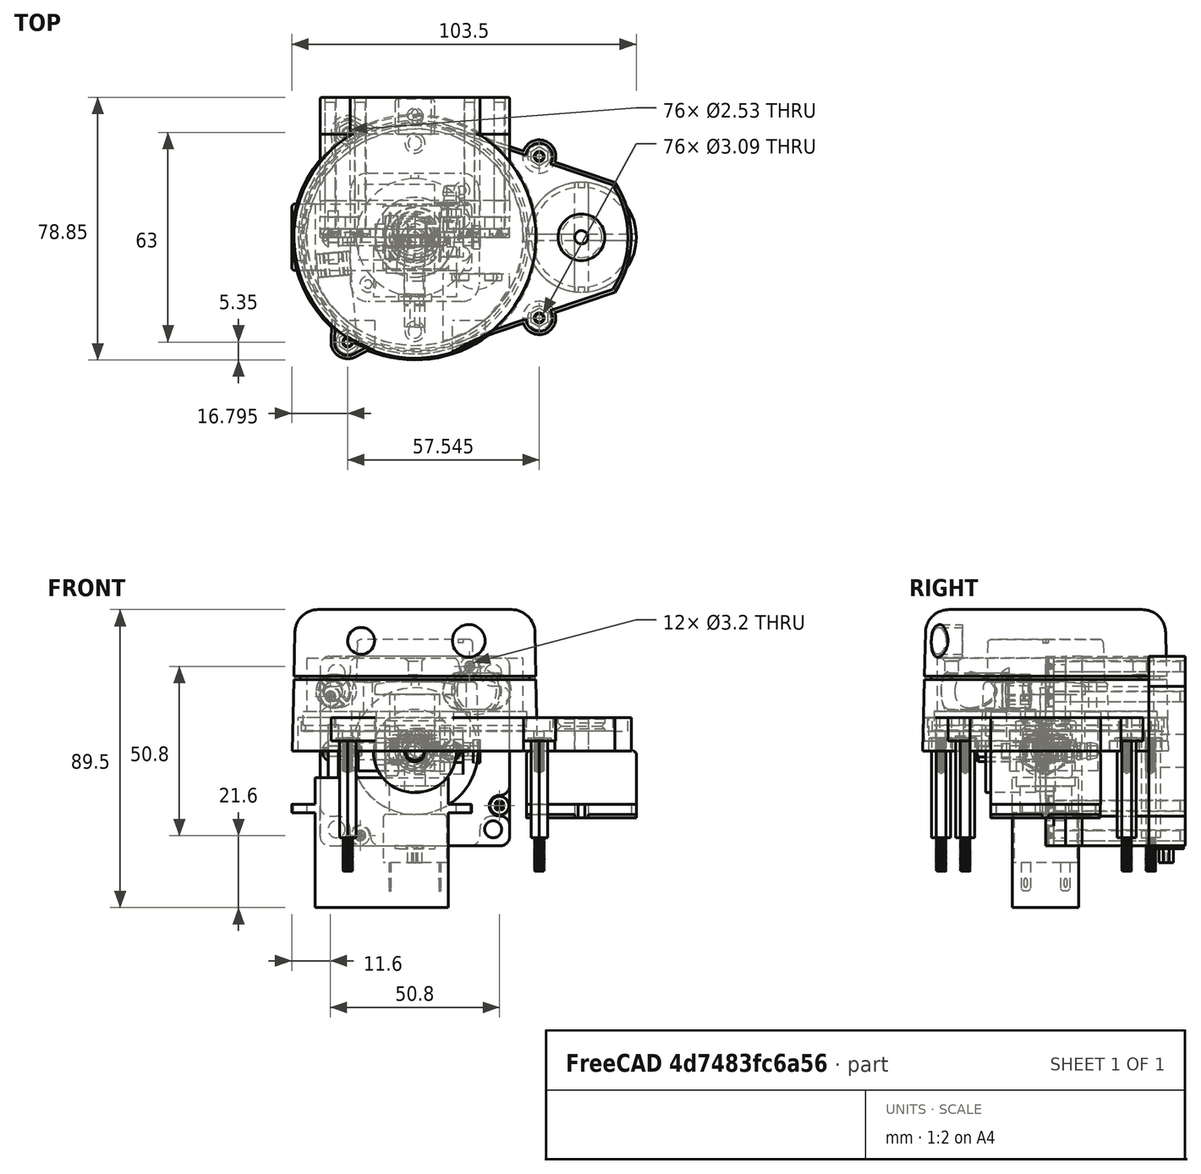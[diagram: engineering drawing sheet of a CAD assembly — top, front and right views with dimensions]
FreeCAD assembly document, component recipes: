
FREECAD ASSEMBLY — COMPONENT RECIPES ("generic-hardware")

This assembly document has 22 components, labeled P0..P21 below (a component is one placed body or linked part). 20 of them carry a construction recipe — the FreeCAD feature program that regenerates the part from scratch, quoted from this document or its linked companion documents; the rest are supplied as boundary geometry only. No exploded tour is included for this assembly.
NOTE — this tour is split across 2 documents so each fits a 32k-token context. This is document 1: the component sections continue in the remaining 1 document, each repeating the header above.
COMPONENT P0 — recipe-attached ("MKS_SERVO57B_", modeled in this document).
Construction recipe (the document's own serialized feature program — sketch geometry with constraints, then the solid features built on it; lengths are millimeters unless a unit is written):

FEATURE [Sketcher::SketchObject] Sketch
  ArcFitTolerance = 0
  AttachmentSupport = -> [XY_Plane]
  ExternalBSplineMaxDegree = 0
  ExternalBSplineTolerance = 0
  FullyConstrained = true
  InternalTolerance = 1e-06
  MakeInternals = false
  MapMode = 5
  Support = -> [XY_Plane]
  TreeRank = 0
  sketch-geometry (8):
    g0: LineSegment StartX=-28 StartY=0 StartZ=0 EndX=-28 EndY=18.5 EndZ=0
    g1: LineSegment StartX=-28 StartY=18.5 StartZ=0 EndX=-18.5 EndY=18.5 EndZ=0
    g2: LineSegment StartX=-18.5 StartY=18.5 StartZ=0 EndX=-18.5 EndY=28 EndZ=0
    g3: LineSegment StartX=-18.5 StartY=28 StartZ=0 EndX=0 EndY=28 EndZ=0
    g4: LineSegment StartX=0 StartY=28 StartZ=0 EndX=0 EndY=0 EndZ=0
    g5: LineSegment StartX=0 StartY=0 StartZ=0 EndX=-28 EndY=0 EndZ=0
    g6: Circle CenterX=-16 CenterY=25.5 CenterZ=0 NormalX=0 NormalY=0 NormalZ=1 AngleXU=0 Radius=1.55
    g7: Circle CenterX=-25.5 CenterY=16 CenterZ=0 NormalX=0 NormalY=0 NormalZ=1 AngleXU=0 Radius=1.55
  constraints (23):
    c: PointOnObject(g0,g-1)
    c: Vertical(g0)
    c: Coincident(g0,g1)
    c: Coincident(g1,g2)
    c: Vertical(g2)
    c: Coincident(g2,g3)
    c: PointOnObject(g3,g-2)
    c: Horizontal(g3)
    c: Coincident(g3,g4)
    c: Coincident(g4,g-1)
    c: Coincident(g4,g5)
    c: Coincident(g5,g0)
    c: Horizontal(g1)
    c: Equal(g2,g1)
    c: DistanceX(g5,g5) = 28
    c: Equal(g4,g5)
    c: DistanceX(g1,g1) = 9.5
    c: Equal(g7,g6)
    c: Diameter(g6) = 3.1
    c: DistanceX(g6) = -16
    c: DistanceY(g6) = 25.5
    c: DistanceX(g7) = -25.5
    c: DistanceY(g7) = 16
FEATURE [PartDesign::Pad] Pad
  AddSubType = 0
  AutoTaperInnerAngle = false
  CheckUpToFaceLimits = true
  ClaimChildren = false
  Direction = (1,1,1)
  Fit = 0
  FitJoin = 0
  InnerFit = 0
  InnerFitJoin = 0
  Length = 20
  Length2 = 100
  NewSolid = false
  Profile = -> Sketch
  Refine = true
  Suppress = false
  TaperInnerAngle = 0
  TaperInnerAngleRev = 0
  TreeRank = 0
  Type = 0
  _ProfileBasedVersion = 0
FEATURE [PartDesign::PolarPattern] PolarPattern012
  AddSubType = 0
  Angle = 360
  Axis = -> Sketch [N_Axis]
  BaseFeature = -> Pad
  CopyShape = false
  NewSolid = false
  Occurrences = 4
  OriginalSubs = -> [Pad]
  Originals = -> [Pad]
  ParallelTransform = true
  Refine = true
  SubTransform = true
  Suppress = false
  TreeRank = 0
  _Version = 0
FEATURE [PartDesign::Fillet] Fillet004
  AddSubType = 0
  Base = -> PolarPattern012 [Edge2,Edge38,Edge11,Edge33]
  BaseFeature = -> PolarPattern012
  NewSolid = false
  Radius = 4
  Refine = true
  SupportTransform = false
  Suppress = false
  TreeRank = 0
FEATURE [PartDesign::Fillet] Fillet005
  AddSubType = 0
  Base = -> Fillet004 [Edge30,Edge58,Edge60,Edge63,Edge61,Edge55,Edge53,Edge3]
  BaseFeature = -> Fillet004
  NewSolid = false
  Radius = 2.5
  Refine = true
  SupportTransform = false
  Suppress = false
  TreeRank = 0
FEATURE [Sketcher::SketchObject] Sketch019
  ArcFitTolerance = 0
  AttachmentSupport = -> [XZ_Plane]
  ExternalBSplineMaxDegree = 0
  ExternalBSplineTolerance = 0
  FullyConstrained = true
  InternalTolerance = 1e-06
  MakeInternals = false
  MapMode = 5
  Placement = pos=(0,0,0) rot=(1,0,0;1.5708rad)
  Support = -> [XZ_Plane]
  TreeRank = 0
  sketch-geometry (4):
    g0: LineSegment StartX=-7 StartY=10 StartZ=0 EndX=11 EndY=10 EndZ=0
    g1: LineSegment StartX=11 StartY=10 StartZ=0 EndX=11 EndY=3.5 EndZ=0
    g2: LineSegment StartX=11 StartY=3.5 StartZ=0 EndX=-7 EndY=3.5 EndZ=0
    g3: LineSegment StartX=-7 StartY=3.5 StartZ=0 EndX=-7 EndY=10 EndZ=0
  constraints (12):
    c: Coincident(g0,g1)
    c: Coincident(g1,g2)
    c: Coincident(g2,g3)
    c: Coincident(g3,g0)
    c: Horizontal(g0)
    c: Horizontal(g2)
    c: Vertical(g1)
    c: Vertical(g3)
    c: DistanceY(g1,g1) = 6.5
    c: DistanceX(g0,g0) = 18
    c: DistanceX(g0) = -7
    c: DistanceY(g0) = 10
FEATURE [PartDesign::Pad] Pad012
  AddSubType = 0
  AutoTaperInnerAngle = false
  BaseFeature = -> Fillet005
  CheckUpToFaceLimits = true
  ClaimChildren = false
  Direction = (1,1,1)
  Fit = 0
  FitJoin = 0
  InnerFit = 0
  InnerFitJoin = 0
  Length = 31.5
  Length2 = 100
  NewSolid = false
  Profile = -> Sketch019
  Refine = true
  Suppress = false
  TaperInnerAngle = 0
  TaperInnerAngleRev = 0
  TreeRank = 0
  Type = 0
  _ProfileBasedVersion = 0
FEATURE [PartDesign::Body] Body  label="MKS_SERVO57B_"
  AutoGroupSolids = false
  ClaimAllChildren = false
  ExportMode = 0
  Group = -> [Sketch,Pad,PolarPattern012,Fillet004,Fillet005,Sketch019,Pad012]
  Origin = -> Origin015
  SingleSolid = true
  Tip = -> Pad012
  TreeRank = 0
  _ExportChildren = -> [Pad,PolarPattern012,Fillet004,Fillet005,Pad012]
  _GroupVersion = 1
COMPONENT P1 — recipe-attached ("Corner", modeled in this document).
Construction recipe (the document's own serialized feature program — sketch geometry with constraints, then the solid features built on it; lengths are millimeters unless a unit is written):

FEATURE [Sketcher::SketchObject] Sketch001
  ArcFitTolerance = 0
  AttachmentSupport = -> [YZ_Plane001]
  ExternalBSplineMaxDegree = 0
  ExternalBSplineTolerance = 0
  FullyConstrained = true
  InternalTolerance = 1e-06
  MakeInternals = false
  MapMode = 5
  Placement = pos=(0,0,0) rot=(0.57735,0.57735,0.57735;2.0944rad)
  Support = -> [YZ_Plane001]
  TreeRank = 0
  sketch-geometry (4):
    g0: LineSegment StartX=-5 StartY=5 StartZ=0 EndX=5 EndY=5 EndZ=0
    g1: LineSegment StartX=5 StartY=5 StartZ=0 EndX=5 EndY=-5 EndZ=0
    g2: LineSegment StartX=5 StartY=-5 StartZ=0 EndX=-5 EndY=-5 EndZ=0
    g3: LineSegment StartX=-5 StartY=-5 StartZ=0 EndX=-5 EndY=5 EndZ=0
  constraints (11):
    c: Coincident(g0,g1)
    c: Coincident(g1,g2)
    c: Coincident(g2,g3)
    c: Coincident(g3,g0)
    c: Horizontal(g0)
    c: Horizontal(g2)
    c: Vertical(g1)
    c: Vertical(g3)
    c: Symmetric(g1,g0,g-1)
    c: Equal(g0,g3)
    c: DistanceX(g0,g0) = 10
FEATURE [PartDesign::Pad] Pad001
  AddSubType = 0
  AutoTaperInnerAngle = false
  CheckUpToFaceLimits = true
  ClaimChildren = false
  Direction = (1,1,1)
  Fit = 0
  FitJoin = 0
  InnerFit = 0
  InnerFitJoin = 0
  Length = 10
  Length2 = 100
  Midplane = true
  NewSolid = false
  Placement = pos=(0,0,0) rot=(0.57735,0.57735,0.57735;2.0944rad)
  Profile = -> Sketch001
  Refine = true
  Suppress = false
  TaperInnerAngle = 0
  TaperInnerAngleRev = 0
  TreeRank = 0
  Type = 0
  _ProfileBasedVersion = 0
FEATURE [Sketcher::SketchObject] Sketch002
  ArcFitTolerance = 0
  AttachmentSupport = -> [YZ_Plane001]
  ExternalBSplineMaxDegree = 0
  ExternalBSplineTolerance = 0
  FullyConstrained = true
  InternalTolerance = 1e-06
  MakeInternals = false
  MapMode = 5
  Placement = pos=(0,0,0) rot=(0.57735,0.57735,0.57735;2.0944rad)
  Support = -> [YZ_Plane001]
  TreeRank = 0
  sketch-geometry (1):
    g0: Circle CenterX=0 CenterY=0 CenterZ=0 NormalX=0 NormalY=0 NormalZ=1 AngleXU=0 Radius=1.5
  constraints (2):
    c: Coincident(g0,g-1)
    c: Diameter(g0) = 3
FEATURE [PartDesign::Pocket] Pocket
  AddSubType = 1
  AutoTaperInnerAngle = false
  BaseFeature = -> Pad001
  CheckUpToFaceLimits = true
  ClaimChildren = false
  Fit = 0
  FitJoin = 0
  InnerFit = 0
  InnerFitJoin = 0
  Length = 5
  Length2 = 100
  Midplane = true
  NewSolid = false
  Placement = pos=(0,0,0) rot=(0.57735,0.57735,0.57735;2.0944rad)
  Profile = -> Sketch002
  Refine = true
  Suppress = false
  TaperInnerAngle = 0
  TaperInnerAngleRev = 0
  TreeRank = 0
  Type = 1
  _ProfileBasedVersion = 0
  _Version = 0
FEATURE [PartDesign::PolarPattern] PolarPattern
  AddSubType = 0
  Angle = 90
  Axis = -> Z_Axis001
  CopyShape = false
  NewSolid = false
  Occurrences = 2
  ParallelTransform = true
  Placement = pos=(0,0,0) rot=(0.57735,0.57735,0.57735;2.0944rad)
  Refine = true
  SubTransform = true
  Suppress = false
  TreeRank = 0
  _Version = 0
FEATURE [PartDesign::PolarPattern] PolarPattern001
  AddSubType = 0
  Angle = 90
  Axis = -> Y_Axis001
  CopyShape = false
  NewSolid = false
  Occurrences = 2
  ParallelTransform = true
  Placement = pos=(0,0,0) rot=(0.57735,0.57735,0.57735;2.0944rad)
  Refine = true
  SubTransform = true
  Suppress = false
  TreeRank = 0
  _Version = 0
FEATURE [PartDesign::MultiTransform] MultiTransform
  AddSubType = 0
  BaseFeature = -> Pocket
  CopyShape = false
  NewSolid = false
  OriginalSubs = -> [Pocket]
  Originals = -> [Pocket]
  ParallelTransform = true
  Placement = pos=(0,0,0) rot=(0.57735,0.57735,0.57735;2.0944rad)
  Refine = true
  SubTransform = true
  Suppress = false
  Transformations = -> [PolarPattern,PolarPattern001]
  TreeRank = 0
  _Version = 0
FEATURE [PartDesign::Plane] DatumPlane
  AttachmentOffset = pos=(0,0,5) rot=(0,0,1;0rad)
  AttachmentSupport = -> [YZ_Plane001]
  Length = 10
  MapMode = 5
  MinimumLength = 10
  MinimumWidth = 10
  Placement = pos=(5,-1.1e-15,1.1e-15) rot=(0.57735,0.57735,0.57735;2.0944rad)
  ResizeMode = 0
  Support = -> [YZ_Plane001]
  TreeRank = 0
  Width = 10
FEATURE [Sketcher::SketchObject] Sketch003
  ArcFitTolerance = 0
  AttachmentSupport = -> [DatumPlane]
  ExternalBSplineMaxDegree = 0
  ExternalBSplineTolerance = 0
  FullyConstrained = true
  InternalTolerance = 1e-06
  MakeInternals = false
  MapMode = 5
  Placement = pos=(5,-1.1e-15,1.1e-15) rot=(0.57735,0.57735,0.57735;2.0944rad)
  Support = -> [DatumPlane]
  TreeRank = 0
  sketch-geometry (1):
    g0: Circle CenterX=0 CenterY=0 CenterZ=0 NormalX=0 NormalY=0 NormalZ=1 AngleXU=0 Radius=3
  constraints (2):
    c: Coincident(g0,g-1)
    c: Diameter(g0) = 6
FEATURE [PartDesign::Pocket] Pocket001
  AddSubType = 1
  AutoTaperInnerAngle = false
  BaseFeature = -> MultiTransform
  CheckUpToFaceLimits = true
  ClaimChildren = false
  Fit = 0
  FitJoin = 0
  InnerFit = 0
  InnerFitJoin = 0
  Length = 8
  Length2 = 100
  NewSolid = false
  Placement = pos=(0,0,0) rot=(0.57735,0.57735,0.57735;2.0944rad)
  Profile = -> Sketch003
  Refine = true
  Suppress = false
  TaperInnerAngle = 0
  TaperInnerAngleRev = 0
  TreeRank = 0
  Type = 0
  _ProfileBasedVersion = 0
  _Version = 0
FEATURE [PartDesign::PolarPattern] PolarPattern002
  AddSubType = 0
  Angle = 90
  Axis = -> Y_Axis001
  CopyShape = false
  NewSolid = false
  Occurrences = 2
  ParallelTransform = true
  Placement = pos=(0,0,0) rot=(0.57735,0.57735,0.57735;2.0944rad)
  Refine = true
  SubTransform = true
  Suppress = false
  TreeRank = 0
  _Version = 0
FEATURE [PartDesign::PolarPattern] PolarPattern003
  AddSubType = 0
  Angle = 90
  Axis = -> Z_Axis001
  CopyShape = false
  NewSolid = false
  Occurrences = 2
  ParallelTransform = true
  Placement = pos=(0,0,0) rot=(0.57735,0.57735,0.57735;2.0944rad)
  Refine = true
  SubTransform = true
  Suppress = false
  TreeRank = 0
  _Version = 0
FEATURE [PartDesign::MultiTransform] MultiTransform001
  AddSubType = 0
  BaseFeature = -> Pocket001
  CopyShape = false
  NewSolid = false
  OriginalSubs = -> [Pocket001]
  Originals = -> [Pocket001]
  ParallelTransform = true
  Placement = pos=(0,0,0) rot=(0.57735,0.57735,0.57735;2.0944rad)
  Refine = true
  SubTransform = true
  Suppress = false
  Transformations = -> [PolarPattern002,PolarPattern003]
  TreeRank = 0
  _Version = 0
FEATURE [PartDesign::Body] Body001  label="Corner"
  AutoGroupSolids = false
  ClaimAllChildren = false
  ExportMode = 0
  Group = -> [Sketch001,Pad001,Sketch002,Pocket,MultiTransform,PolarPattern,PolarPattern001,DatumPlane,Sketch003,Pocket001,MultiTransform001,PolarPattern002,PolarPattern003]
  Origin = -> Origin001
  SingleSolid = true
  Tip = -> MultiTransform001
  TreeRank = 0
  _ExportChildren = -> [Pad001,Pocket,MultiTransform,DatumPlane,Pocket001,MultiTransform001]
  _GroupVersion = 1
COMPONENT P2 — recipe-attached ("MB_100", modeled in this document).
Construction recipe (the document's own serialized feature program — sketch geometry with constraints, then the solid features built on it; lengths are millimeters unless a unit is written):

FEATURE [Sketcher::SketchObject] Sketch004
  ArcFitTolerance = 0
  AttachmentSupport = -> [XZ_Plane002]
  ExternalBSplineMaxDegree = 0
  ExternalBSplineTolerance = 0
  FullyConstrained = true
  InternalTolerance = 1e-06
  MakeInternals = false
  MapMode = 5
  Placement = pos=(0,0,0) rot=(1,0,0;1.5708rad)
  Support = -> [XZ_Plane002]
  TreeRank = 0
  sketch-geometry (14):
    g0: ArcOfCircle CenterX=0 CenterY=0 CenterZ=0 NormalX=0 NormalY=0 NormalZ=1 AngleXU=0 Radius=1.25 StartAngle=0 EndAngle=1.5708
    g1: LineSegment StartX=1e-16 StartY=1.25 StartZ=0 EndX=0 EndY=2 EndZ=0
    g2: LineSegment StartX=0 StartY=2 StartZ=0 EndX=1 EndY=2 EndZ=0
    g3: LineSegment [constr] StartX=0 StartY=0 StartZ=0 EndX=5 EndY=5 EndZ=0
    g4: LineSegment StartX=1 StartY=2 StartZ=0 EndX=3.3 EndY=4 EndZ=0
    g5: LineSegment StartX=3.3 StartY=4 StartZ=0 EndX=1.5 EndY=4 EndZ=0
    g6: LineSegment StartX=1.5 StartY=4 StartZ=0 EndX=1.5 EndY=5 EndZ=0
    g7: LineSegment StartX=1.5 StartY=5 StartZ=0 EndX=5 EndY=5 EndZ=0
    g8: LineSegment StartX=5 StartY=5 StartZ=0 EndX=5 EndY=1.5 EndZ=0
    g9: LineSegment StartX=5 StartY=1.5 StartZ=0 EndX=4 EndY=1.5 EndZ=0
    g10: LineSegment StartX=4 StartY=1.5 StartZ=0 EndX=4 EndY=3.3 EndZ=0
    g11: LineSegment StartX=4 StartY=3.3 StartZ=0 EndX=2 EndY=1 EndZ=0
    g12: LineSegment StartX=2 StartY=1 StartZ=0 EndX=2 EndY=0 EndZ=0
    g13: LineSegment StartX=2 StartY=0 StartZ=0 EndX=1.25 EndY=0 EndZ=0
  constraints (41):
    c: Coincident(g0,g-1)
    c: PointOnObject(g0,g-1)
    c: PointOnObject(g0,g-2)
    c: Coincident(g1,g0)
    c: PointOnObject(g1,g-2)
    c: Coincident(g2,g1)
    c: Horizontal(g2)
    c: Coincident(g3,g0)
    c: Angle(g-1,g3) = 0.785398
    c: DistanceX(g3) = 5
    c: Diameter(g0) = 2.5
    c: DistanceX(g2) = 1
    c: Coincident(g4,g2)
    c: Coincident(g5,g4)
    c: Horizontal(g5)
    c: Coincident(g6,g5)
    c: Vertical(g6)
    c: Coincident(g7,g6)
    c: Coincident(g7,g3)
    c: Coincident(g8,g7)
    c: Vertical(g8)
    c: Coincident(g9,g8)
    c: Coincident(g10,g9)
    c: Vertical(g10)
    c: Coincident(g11,g10)
    c: Coincident(g12,g11)
    c: PointOnObject(g12,g-1)
    c: Vertical(g12)
    c: Coincident(g13,g12)
    c: Coincident(g13,g0)
    c: Equal(g12,g2)
    c: Equal(g13,g1)
    c: Horizontal(g7)
    c: Horizontal(g9)
    c: Equal(g6,g9)
    c: Equal(g11,g4)
    c: Equal(g5,g10)
    c: DistanceY(g2,g6) = 3
    c: DistanceX(g6) = 1.5
    c: DistanceY(g6,g6) = 1
    c: DistanceX(g5,g5) = 1.8
FEATURE [PartDesign::Pad] Pad002
  AddSubType = 0
  AutoTaperInnerAngle = false
  CheckUpToFaceLimits = true
  ClaimChildren = false
  Direction = (1,1,1)
  Fit = 0
  FitJoin = 0
  InnerFit = 0
  InnerFitJoin = 0
  Length = 100
  Length2 = 100
  NewSolid = false
  Placement = pos=(0,0,0) rot=(1,0,0;1.5708rad)
  Profile = -> Sketch004
  Refine = true
  Reversed = true
  Suppress = false
  TaperInnerAngle = 0
  TaperInnerAngleRev = 0
  TreeRank = 0
  Type = 0
  _ProfileBasedVersion = 0
FEATURE [PartDesign::PolarPattern] PolarPattern004
  AddSubType = 0
  Angle = 360
  Axis = -> Y_Axis002
  BaseFeature = -> Pad002
  CopyShape = false
  NewSolid = false
  Occurrences = 4
  OriginalSubs = -> [Pad002]
  Originals = -> [Pad002]
  ParallelTransform = true
  Placement = pos=(0,0,0) rot=(1,0,0;1.5708rad)
  Refine = true
  SubTransform = true
  Suppress = false
  TreeRank = 0
  _Version = 0
FEATURE [PartDesign::CoordinateSystem] Local_CS
  AttacherType = Attacher::AttachEngine3D
  AttachmentSupport = -> [PolarPattern004]
  Placement = pos=(4.44e-14,100,0) rot=(1,0,0;1.5708rad)
  Support = -> [PolarPattern004]
  TreeRank = 0
FEATURE [PartDesign::Body] Body002  label="MB_100"
  AutoGroupSolids = false
  ClaimAllChildren = false
  ExportMode = 0
  Group = -> [Sketch004,Pad002,PolarPattern004,Local_CS]
  Origin = -> Origin002
  SingleSolid = true
  Tip = -> PolarPattern004
  TreeRank = 0
  _ExportChildren = -> [Pad002,PolarPattern004,Local_CS]
  _GroupVersion = 1
COMPONENT P3 — recipe-attached ("MB_60", modeled in this document).
Construction recipe (the document's own serialized feature program — sketch geometry with constraints, then the solid features built on it; lengths are millimeters unless a unit is written):

FEATURE [Sketcher::SketchObject] Sketch005
  ArcFitTolerance = 0
  AttachmentSupport = -> [XZ_Plane003]
  ExternalBSplineMaxDegree = 0
  ExternalBSplineTolerance = 0
  FullyConstrained = true
  InternalTolerance = 1e-06
  MakeInternals = false
  MapMode = 5
  Placement = pos=(0,0,0) rot=(1,0,0;1.5708rad)
  Support = -> [XZ_Plane003]
  TreeRank = 0
  sketch-geometry (14):
    g0: ArcOfCircle CenterX=0 CenterY=0 CenterZ=0 NormalX=0 NormalY=0 NormalZ=1 AngleXU=0 Radius=1.25 StartAngle=0 EndAngle=1.5708
    g1: LineSegment StartX=1e-16 StartY=1.25 StartZ=0 EndX=0 EndY=2 EndZ=0
    g2: LineSegment StartX=0 StartY=2 StartZ=0 EndX=1 EndY=2 EndZ=0
    g3: LineSegment [constr] StartX=0 StartY=0 StartZ=0 EndX=5 EndY=5 EndZ=0
    g4: LineSegment StartX=1 StartY=2 StartZ=0 EndX=3.3 EndY=4 EndZ=0
    g5: LineSegment StartX=3.3 StartY=4 StartZ=0 EndX=1.5 EndY=4 EndZ=0
    g6: LineSegment StartX=1.5 StartY=4 StartZ=0 EndX=1.5 EndY=5 EndZ=0
    g7: LineSegment StartX=1.5 StartY=5 StartZ=0 EndX=5 EndY=5 EndZ=0
    g8: LineSegment StartX=5 StartY=5 StartZ=0 EndX=5 EndY=1.5 EndZ=0
    g9: LineSegment StartX=5 StartY=1.5 StartZ=0 EndX=4 EndY=1.5 EndZ=0
    g10: LineSegment StartX=4 StartY=1.5 StartZ=0 EndX=4 EndY=3.3 EndZ=0
    g11: LineSegment StartX=4 StartY=3.3 StartZ=0 EndX=2 EndY=1 EndZ=0
    g12: LineSegment StartX=2 StartY=1 StartZ=0 EndX=2 EndY=0 EndZ=0
    g13: LineSegment StartX=2 StartY=0 StartZ=0 EndX=1.25 EndY=0 EndZ=0
  constraints (41):
    c: Coincident(g0,g-1)
    c: PointOnObject(g0,g-1)
    c: PointOnObject(g0,g-2)
    c: Coincident(g1,g0)
    c: PointOnObject(g1,g-2)
    c: Coincident(g2,g1)
    c: Horizontal(g2)
    c: Coincident(g3,g0)
    c: Angle(g-1,g3) = 0.785398
    c: DistanceX(g3) = 5
    c: Diameter(g0) = 2.5
    c: DistanceX(g2) = 1
    c: Coincident(g4,g2)
    c: Coincident(g5,g4)
    c: Horizontal(g5)
    c: Coincident(g6,g5)
    c: Vertical(g6)
    c: Coincident(g7,g6)
    c: Coincident(g7,g3)
    c: Coincident(g8,g7)
    c: Vertical(g8)
    c: Coincident(g9,g8)
    c: Coincident(g10,g9)
    c: Vertical(g10)
    c: Coincident(g11,g10)
    c: Coincident(g12,g11)
    c: PointOnObject(g12,g-1)
    c: Vertical(g12)
    c: Coincident(g13,g12)
    c: Coincident(g13,g0)
    c: Equal(g12,g2)
    c: Equal(g13,g1)
    c: Horizontal(g7)
    c: Horizontal(g9)
    c: Equal(g6,g9)
    c: Equal(g11,g4)
    c: Equal(g5,g10)
    c: DistanceY(g2,g6) = 3
    c: DistanceX(g6) = 1.5
    c: DistanceY(g6,g6) = 1
    c: DistanceX(g5,g5) = 1.8
FEATURE [PartDesign::Pad] Pad003
  AddSubType = 0
  AutoTaperInnerAngle = false
  CheckUpToFaceLimits = true
  ClaimChildren = false
  Direction = (1,1,1)
  Fit = 0
  FitJoin = 0
  InnerFit = 0
  InnerFitJoin = 0
  Length = 60
  Length2 = 100
  NewSolid = false
  Placement = pos=(0,0,0) rot=(1,0,0;1.5708rad)
  Profile = -> Sketch005
  Refine = true
  Reversed = true
  Suppress = false
  TaperInnerAngle = 0
  TaperInnerAngleRev = 0
  TreeRank = 0
  Type = 0
  _ProfileBasedVersion = 0
FEATURE [PartDesign::PolarPattern] PolarPattern005
  AddSubType = 0
  Angle = 360
  AttacherType = Attacher::AttachEngine3D
  Axis = -> Y_Axis003
  BaseFeature = -> Pad003
  CopyShape = false
  NewSolid = false
  Occurrences = 4
  OriginalSubs = -> [Pad003]
  Originals = -> [Pad003]
  ParallelTransform = true
  Placement = pos=(0,0,0) rot=(1,0,0;1.5708rad)
  Refine = true
  SubTransform = true
  Suppress = false
  TreeRank = 0
  _Version = 0
FEATURE [PartDesign::CoordinateSystem] Local_CS001
  AttacherType = Attacher::AttachEngine3D
  AttachmentSupport = -> [PolarPattern005]
  MapMode = 11
  Placement = pos=(2.66e-14,60,-1.33e-14) rot=(1,0,0;1.5708rad)
  Support = -> [PolarPattern005]
  TreeRank = 0
FEATURE [PartDesign::Body] Body003  label="MB_60"
  AutoGroupSolids = false
  ClaimAllChildren = false
  ExportMode = 0
  Group = -> [Sketch005,Pad003,PolarPattern005,Local_CS001]
  Origin = -> Origin003
  SingleSolid = true
  Tip = -> PolarPattern005
  TreeRank = 0
  _ExportChildren = -> [Pad003,PolarPattern005,Local_CS001]
  _GroupVersion = 1
COMPONENT P4 — recipe-attached ("MB_300", modeled in this document).
Construction recipe (the document's own serialized feature program — sketch geometry with constraints, then the solid features built on it; lengths are millimeters unless a unit is written):

FEATURE [Sketcher::SketchObject] Sketch006
  ArcFitTolerance = 0
  AttachmentSupport = -> [XZ_Plane004]
  ExternalBSplineMaxDegree = 0
  ExternalBSplineTolerance = 0
  FullyConstrained = true
  InternalTolerance = 1e-06
  MakeInternals = false
  MapMode = 5
  Placement = pos=(0,0,0) rot=(1,0,0;1.5708rad)
  Support = -> [XZ_Plane004]
  TreeRank = 0
  sketch-geometry (14):
    g0: ArcOfCircle CenterX=0 CenterY=0 CenterZ=0 NormalX=0 NormalY=0 NormalZ=1 AngleXU=0 Radius=1.25 StartAngle=0 EndAngle=1.5708
    g1: LineSegment StartX=1e-16 StartY=1.25 StartZ=0 EndX=0 EndY=2 EndZ=0
    g2: LineSegment StartX=0 StartY=2 StartZ=0 EndX=1 EndY=2 EndZ=0
    g3: LineSegment [constr] StartX=0 StartY=0 StartZ=0 EndX=5 EndY=5 EndZ=0
    g4: LineSegment StartX=1 StartY=2 StartZ=0 EndX=3.3 EndY=4 EndZ=0
    g5: LineSegment StartX=3.3 StartY=4 StartZ=0 EndX=1.5 EndY=4 EndZ=0
    g6: LineSegment StartX=1.5 StartY=4 StartZ=0 EndX=1.5 EndY=5 EndZ=0
    g7: LineSegment StartX=1.5 StartY=5 StartZ=0 EndX=5 EndY=5 EndZ=0
    g8: LineSegment StartX=5 StartY=5 StartZ=0 EndX=5 EndY=1.5 EndZ=0
    g9: LineSegment StartX=5 StartY=1.5 StartZ=0 EndX=4 EndY=1.5 EndZ=0
    g10: LineSegment StartX=4 StartY=1.5 StartZ=0 EndX=4 EndY=3.3 EndZ=0
    g11: LineSegment StartX=4 StartY=3.3 StartZ=0 EndX=2 EndY=1 EndZ=0
    g12: LineSegment StartX=2 StartY=1 StartZ=0 EndX=2 EndY=0 EndZ=0
    g13: LineSegment StartX=2 StartY=0 StartZ=0 EndX=1.25 EndY=0 EndZ=0
  constraints (41):
    c: Coincident(g0,g-1)
    c: PointOnObject(g0,g-1)
    c: PointOnObject(g0,g-2)
    c: Coincident(g1,g0)
    c: PointOnObject(g1,g-2)
    c: Coincident(g2,g1)
    c: Horizontal(g2)
    c: Coincident(g3,g0)
    c: Angle(g-1,g3) = 0.785398
    c: DistanceX(g3) = 5
    c: Diameter(g0) = 2.5
    c: DistanceX(g2) = 1
    c: Coincident(g4,g2)
    c: Coincident(g5,g4)
    c: Horizontal(g5)
    c: Coincident(g6,g5)
    c: Vertical(g6)
    c: Coincident(g7,g6)
    c: Coincident(g7,g3)
    c: Coincident(g8,g7)
    c: Vertical(g8)
    c: Coincident(g9,g8)
    c: Coincident(g10,g9)
    c: Vertical(g10)
    c: Coincident(g11,g10)
    c: Coincident(g12,g11)
    c: PointOnObject(g12,g-1)
    c: Vertical(g12)
    c: Coincident(g13,g12)
    c: Coincident(g13,g0)
    c: Equal(g12,g2)
    c: Equal(g13,g1)
    c: Horizontal(g7)
    c: Horizontal(g9)
    c: Equal(g6,g9)
    c: Equal(g11,g4)
    c: Equal(g5,g10)
    c: DistanceY(g2,g6) = 3
    c: DistanceX(g6) = 1.5
    c: DistanceY(g6,g6) = 1
    c: DistanceX(g5,g5) = 1.8
FEATURE [PartDesign::Pad] Pad004
  AddSubType = 0
  AutoTaperInnerAngle = false
  CheckUpToFaceLimits = true
  ClaimChildren = false
  Direction = (1,1,1)
  Fit = 0
  FitJoin = 0
  InnerFit = 0
  InnerFitJoin = 0
  Length = 300
  Length2 = 100
  NewSolid = false
  Placement = pos=(0,0,0) rot=(1,0,0;1.5708rad)
  Profile = -> Sketch006
  Refine = true
  Reversed = true
  Suppress = false
  TaperInnerAngle = 0
  TaperInnerAngleRev = 0
  TreeRank = 0
  Type = 0
  _ProfileBasedVersion = 0
FEATURE [PartDesign::PolarPattern] PolarPattern006
  AddSubType = 0
  Angle = 360
  Axis = -> Y_Axis004
  BaseFeature = -> Pad004
  CopyShape = false
  NewSolid = false
  Occurrences = 4
  OriginalSubs = -> [Pad004]
  Originals = -> [Pad004]
  ParallelTransform = true
  Placement = pos=(0,0,0) rot=(1,0,0;1.5708rad)
  Refine = true
  SubTransform = true
  Suppress = false
  TreeRank = 0
  _Version = 0
FEATURE [PartDesign::CoordinateSystem] Local_CS002
  AttacherType = Attacher::AttachEngine3D
  AttachmentSupport = -> [PolarPattern006]
  MapMode = 11
  Placement = pos=(1.332e-13,300,-6.66e-14) rot=(1,0,0;1.5708rad)
  Support = -> [PolarPattern006]
  TreeRank = 0
FEATURE [PartDesign::Body] Body004  label="MB_300"
  AutoGroupSolids = false
  ClaimAllChildren = false
  ExportMode = 0
  Group = -> [Sketch006,Pad004,PolarPattern006,Local_CS002]
  Origin = -> Origin004
  SingleSolid = true
  Tip = -> PolarPattern006
  TreeRank = 0
  _ExportChildren = -> [Pad004,PolarPattern006,Local_CS002]
  _GroupVersion = 1
COMPONENT P5 — recipe-attached ("ServoPalonnier", modeled in this document).
Construction recipe (the document's own serialized feature program — sketch geometry with constraints, then the solid features built on it; lengths are millimeters unless a unit is written):

FEATURE [Sketcher::SketchObject] Sketch088
  ArcFitTolerance = 0
  AttachmentSupport = -> [XY_Plane050]
  ExternalBSplineMaxDegree = 0
  ExternalBSplineTolerance = 0
  FullyConstrained = true
  InternalTolerance = 1e-06
  MakeInternals = false
  MapMode = 5
  Support = -> [XY_Plane050]
  TreeRank = 0
  sketch-geometry (7):
    g0: Circle CenterX=0 CenterY=0 CenterZ=0 NormalX=0 NormalY=0 NormalZ=1 AngleXU=0 Radius=10
    g1: Circle CenterX=0 CenterY=7 CenterZ=0 NormalX=0 NormalY=0 NormalZ=1 AngleXU=0 Radius=1.5
    g2: Circle CenterX=7 CenterY=0 CenterZ=0 NormalX=0 NormalY=0 NormalZ=1 AngleXU=0 Radius=1.5
    g3: Circle CenterX=0 CenterY=-7 CenterZ=0 NormalX=0 NormalY=0 NormalZ=1 AngleXU=0 Radius=1.5
    g4: Circle CenterX=-7 CenterY=0 CenterZ=0 NormalX=0 NormalY=0 NormalZ=1 AngleXU=0 Radius=1.5
    g5: Circle [constr] CenterX=0 CenterY=0 CenterZ=0 NormalX=0 NormalY=0 NormalZ=1 AngleXU=0 Radius=7
    g6: Circle CenterX=0 CenterY=0 CenterZ=0 NormalX=0 NormalY=0 NormalZ=1 AngleXU=0 Radius=1.5
  constraints (18):
    c: Coincident(g0,g-1)
    c: Diameter(g0) = 20
    c: PointOnObject(g1,g-2)
    c: PointOnObject(g2,g-1)
    c: PointOnObject(g3,g-2)
    c: PointOnObject(g4,g-1)
    c: Equal(g4,g1)
    c: Equal(g1,g2)
    c: Equal(g2,g3)
    c: Diameter(g1) = 3
    c: Coincident(g5,g0)
    c: PointOnObject(g1,g5)
    c: PointOnObject(g2,g5)
    c: PointOnObject(g3,g5)
    c: PointOnObject(g4,g5)
    c: DistanceX(g4,g2) = 14
    c: Coincident(g6,g0)
    c: Equal(g2,g6)
FEATURE [PartDesign::Pad] Pad052
  AddSubType = 0
  AutoTaperInnerAngle = false
  CheckUpToFaceLimits = true
  ClaimChildren = false
  Direction = (1,1,1)
  Fit = 0
  FitJoin = 0
  InnerFit = 0
  InnerFitJoin = 0
  Length = 2
  Length2 = 100
  Linearize = true
  NewSolid = false
  Profile = -> Sketch088
  Refine = true
  Reversed = true
  Suppress = false
  TaperInnerAngle = 0
  TaperInnerAngleRev = 0
  TreeRank = 0
  Type = 0
  _ProfileBasedVersion = 1
FEATURE [Sketcher::SketchObject] Sketch089
  ArcFitTolerance = 0
  AttachmentSupport = -> [XY_Plane050]
  ExternalBSplineMaxDegree = 0
  ExternalBSplineTolerance = 0
  FullyConstrained = true
  InternalTolerance = 1e-06
  MakeInternals = false
  MapMode = 5
  Support = -> [XY_Plane050]
  TreeRank = 0
  sketch-geometry (2):
    g0: Circle CenterX=0 CenterY=0 CenterZ=0 NormalX=0 NormalY=0 NormalZ=1 AngleXU=0 Radius=4.7
    g1: Circle CenterX=0 CenterY=0 CenterZ=0 NormalX=0 NormalY=0 NormalZ=1 AngleXU=0 Radius=3
  constraints (4):
    c: Coincident(g0,g-1)
    c: Coincident(g1,g0)
    c: Diameter(g0) = 9.4
    c: Diameter(g1) = 6
FEATURE [PartDesign::Pad] Pad051
  AddSubType = 0
  AutoTaperInnerAngle = false
  BaseFeature = -> Pad052
  CheckUpToFaceLimits = true
  ClaimChildren = false
  Direction = (1,1,1)
  Fit = 0
  FitJoin = 0
  InnerFit = 0
  InnerFitJoin = 0
  Length = 5.4
  Length2 = 100
  Linearize = true
  NewSolid = false
  Profile = -> Sketch089
  Refine = true
  Reversed = true
  Suppress = false
  TaperInnerAngle = 0
  TaperInnerAngleRev = 0
  TreeRank = 0
  Type = 0
  _ProfileBasedVersion = 1
FEATURE [PartDesign::Body] Body042  label="ServoPalonnier"
  AutoGroupSolids = false
  ClaimAllChildren = false
  ExportMode = 0
  Group = -> [Sketch088,Pad052,Sketch089,Pad051]
  Origin = -> Origin063
  Placement = pos=(0,0,0) rot=(1,0,0;1.5708rad)
  SingleSolid = true
  Tip = -> Pad051
  TreeRank = 0
  _ExportChildren = -> [Pad052,Pad051]
  _GroupVersion = 1
COMPONENT P6 — recipe-attached ("PalonnierElastique", modeled in this document).
Construction recipe (the document's own serialized feature program — sketch geometry with constraints, then the solid features built on it; lengths are millimeters unless a unit is written):

FEATURE [Sketcher::SketchObject] Sketch123
  ArcFitTolerance = 0
  AttachmentSupport = -> [XZ_Plane068]
  ExternalBSplineMaxDegree = 0
  ExternalBSplineTolerance = 0
  FullyConstrained = false
  InternalTolerance = 1e-06
  MakeInternals = false
  MapMode = 5
  Placement = pos=(0,0,0) rot=(1,0,0;1.5708rad)
  Support = -> [XZ_Plane068]
  TreeRank = 0
  sketch-geometry (17):
    g0: ArcOfCircle CenterX=0 CenterY=0 CenterZ=0 NormalX=0 NormalY=0 NormalZ=1 AngleXU=0 Radius=8 StartAngle=5.67415 EndAngle=10.0338
    g1: ArcOfCircle CenterX=-2e-15 CenterY=1 CenterZ=0 NormalX=0 NormalY=0 NormalZ=1 AngleXU=0 Radius=26 StartAngle=4.4405 EndAngle=4.98428
    g2: ArcOfCircle CenterX=6.42512 CenterY=-22.0462 CenterZ=0 NormalX=0 NormalY=0 NormalZ=1 AngleXU=0 Radius=2.07488 StartAngle=4.98428 EndAngle=6.60035
    g3: ArcOfCircle CenterX=-6.42512 CenterY=-22.0462 CenterZ=0 NormalX=0 NormalY=0 NormalZ=1 AngleXU=0 Radius=2.07488 StartAngle=2.82442 EndAngle=4.4405
    g4: LineSegment [constr] StartX=8.5 StartY=0 StartZ=0 EndX=8.5 EndY=-36.4357 EndZ=0
    g5: GeomPoint [constr] X=0 Y=-25 Z=0
    g6: GeomPoint [constr] X=0 Y=8 Z=0
    g7: Circle CenterX=-5.5 CenterY=-21 CenterZ=0 NormalX=0 NormalY=0 NormalZ=1 AngleXU=0 Radius=1.5
    g8: Circle CenterX=0 CenterY=-21 CenterZ=0 NormalX=0 NormalY=0 NormalZ=1 AngleXU=0 Radius=1.5
    g9: Circle CenterX=5.5 CenterY=-21 CenterZ=0 NormalX=0 NormalY=0 NormalZ=1 AngleXU=0 Radius=1.5
    g10: Circle CenterX=-4 CenterY=-17 CenterZ=0 NormalX=0 NormalY=0 NormalZ=1 AngleXU=0 Radius=1.5
    g11: Circle CenterX=4 CenterY=-17 CenterZ=0 NormalX=0 NormalY=0 NormalZ=1 AngleXU=0 Radius=1.5
    g12: LineSegment StartX=8.39651 StartY=-21.3991 StartZ=0 EndX=5.42128 EndY=-12.3352 EndZ=0
    g13: LineSegment StartX=-8.39651 StartY=-21.3991 StartZ=0 EndX=-5.42128 EndY=-12.3352 EndZ=0
    g14: ArcOfCircle CenterX=-13.7607 CenterY=-9.59779 CenterZ=0 NormalX=0 NormalY=0 NormalZ=1 AngleXU=0 Radius=8.77717 StartAngle=5.96602 EndAngle=6.89222
    g15: ArcOfCircle CenterX=13.7607 CenterY=-9.59779 CenterZ=0 NormalX=0 NormalY=0 NormalZ=1 AngleXU=0 Radius=8.77717 StartAngle=2.53256 EndAngle=3.45876
    g16: LineSegment [constr] StartX=-5 StartY=-9.05974 StartZ=0 EndX=5 EndY=-9.05974 EndZ=0
  constraints (42):
    c: Coincident(g0,g-1)
    c: Diameter(g0) = 16
    c: Symmetric(g1,g1,g-2)
    c: Symmetric(g0,g0,g-2)
    c: Tangent(g3,g1) = -1.5708
    c: Tangent(g2,g1) = -1.5708
    c: Symmetric(g3,g2,g-2)
    c: PointOnObject(g4,g-1)
    c: Vertical(g4)
    c: Tangent(g2,g4)
    c: DistanceX(g4) = 8.5
    c: PointOnObject(g5,g1)
    c: PointOnObject(g6,g0)
    c: PointOnObject(g6,g-2)
    c: PointOnObject(g5,g-2)
    c: DistanceY(g5,g6) = 33
    c: PointOnObject(g8,g-2)
    c: Horizontal(g7,g8)
    c: Symmetric(g10,g11,g-2)
    c: Symmetric(g7,g9,g-2)
    c: DistanceY(g11) = -17
    c: DistanceY(g9) = -21
    c: Diameter(g7) = 3
    c: Equal(g7,g10)
    c: Equal(g7,g8)
    c: Equal(g7,g9)
    c: Equal(g7,g11)
    c: DistanceX(g7,g9) = 11
    c: DistanceX(g10,g11) = 8
    c: Tangent(g13,g3) = 1.5708
    c: Tangent(g12,g2) = -1.5708
    c: Symmetric(g12,g13,g-2)
    c: Tangent(g15,g12) = 1.5708
    c: Tangent(g15,g0) = 1.5708
    c: PointOnObject(g16,g14)
    c: Horizontal(g16)
    c: PointOnObject(g16,g15)
    c: DistanceX(g16,g16) = 10
    c: Tangent(g14,g13) = -1.5708
    c: Tangent(g14,g0) = 1.5708
    c: Distance(g2,g1) = 3
    c: Diameter(g1) = 52
FEATURE [PartDesign::Pad] Pad066
  AddSubType = 0
  AutoTaperInnerAngle = false
  CheckUpToFaceLimits = true
  ClaimChildren = false
  Direction = (1,1,1)
  Fit = 0
  FitJoin = 0
  InnerFit = 0
  InnerFitJoin = 0
  Length = 4
  Length2 = 100
  Linearize = true
  NewSolid = false
  Placement = pos=(0,0,0) rot=(1,0,0;1.5708rad)
  Profile = -> Sketch123
  Refine = true
  Reversed = true
  Suppress = false
  TaperInnerAngle = 0
  TaperInnerAngleRev = 0
  TreeRank = 0
  Type = 0
  _ProfileBasedVersion = 1
FEATURE [Sketcher::SketchObject] Sketch124
  ArcFitTolerance = 0
  AttachmentSupport = -> [XZ_Plane068]
  ExternalBSplineMaxDegree = 0
  ExternalBSplineTolerance = 0
  FullyConstrained = true
  InternalTolerance = 1e-06
  MakeInternals = false
  MapMode = 5
  Placement = pos=(0,0,0) rot=(1,0,0;1.5708rad)
  Support = -> [XZ_Plane068]
  TreeRank = 0
  sketch-geometry (1):
    g0: Circle CenterX=0 CenterY=0 CenterZ=0 NormalX=0 NormalY=0 NormalZ=1 AngleXU=0 Radius=8
  constraints (2):
    c: Coincident(g0,g-1)
    c: Diameter(g0) = 16
FEATURE [PartDesign::Pad] Pad067
  AddSubType = 0
  AutoTaperInnerAngle = false
  BaseFeature = -> Pad066
  CheckUpToFaceLimits = true
  ClaimChildren = false
  Direction = (1,1,1)
  Fit = 0
  FitJoin = 0
  InnerFit = 0
  InnerFitJoin = 0
  Length = 10
  Length2 = 100
  Linearize = true
  NewSolid = false
  Placement = pos=(0,0,0) rot=(1,0,0;1.5708rad)
  Profile = -> Sketch124
  Refine = true
  Reversed = true
  Suppress = false
  TaperInnerAngle = 0
  TaperInnerAngleRev = 0
  TreeRank = 0
  Type = 0
  _ProfileBasedVersion = 1
FEATURE [Sketcher::SketchObject] Sketch125
  ArcFitTolerance = 0
  AttachmentSupport = -> [Pad067]
  ExternalBSplineMaxDegree = 0
  ExternalBSplineTolerance = 0
  FullyConstrained = true
  InternalTolerance = 1e-06
  MakeInternals = false
  MapMode = 5
  Placement = pos=(0,10,2.2e-15) rot=(-1,0,0;1.5708rad)
  Support = -> [Pad067]
  TreeRank = 0
  sketch-geometry (1):
    g0: Circle CenterX=0 CenterY=0 CenterZ=0 NormalX=0 NormalY=0 NormalZ=1 AngleXU=0 Radius=3
  constraints (2):
    c: Coincident(g0,g-1)
    c: Diameter(g0) = 6
FEATURE [PartDesign::Pocket] Pocket049
  AddSubType = 1
  AutoTaperInnerAngle = false
  BaseFeature = -> Pad067
  CheckUpToFaceLimits = true
  ClaimChildren = false
  Fit = 0
  FitJoin = 0
  InnerFit = 0
  InnerFitJoin = 0
  Length = 3.2
  Length2 = 100
  Linearize = true
  NewSolid = false
  Placement = pos=(0,0,0) rot=(1,0,0;1.5708rad)
  Profile = -> Sketch125
  Refine = true
  Suppress = false
  TaperInnerAngle = 0
  TaperInnerAngleRev = 0
  TreeRank = 0
  Type = 0
  _ProfileBasedVersion = 1
  _Version = 1
FEATURE [Sketcher::SketchObject] Sketch126
  ArcFitTolerance = 0
  AttachmentSupport = -> [XZ_Plane068]
  ExternalBSplineMaxDegree = 0
  ExternalBSplineTolerance = 0
  FullyConstrained = true
  InternalTolerance = 1e-06
  MakeInternals = false
  MapMode = 5
  Placement = pos=(0,0,0) rot=(1,0,0;1.5708rad)
  Support = -> [XZ_Plane068]
  TreeRank = 0
  sketch-geometry (1):
    g0: Circle CenterX=0 CenterY=0 CenterZ=0 NormalX=0 NormalY=0 NormalZ=1 AngleXU=0 Radius=1.5
  constraints (2):
    c: Coincident(g0,g-1)
    c: Diameter(g0) = 3
FEATURE [PartDesign::Pocket] Pocket050
  AddSubType = 1
  AutoTaperInnerAngle = false
  BaseFeature = -> Pocket049
  CheckUpToFaceLimits = true
  ClaimChildren = false
  Fit = 0
  FitJoin = 0
  InnerFit = 0
  InnerFitJoin = 0
  Length = 5
  Length2 = 100
  Linearize = true
  NewSolid = false
  Placement = pos=(0,0,0) rot=(1,0,0;1.5708rad)
  Profile = -> Sketch126
  Refine = true
  Suppress = false
  TaperInnerAngle = 0
  TaperInnerAngleRev = 0
  TreeRank = 0
  Type = 1
  _ProfileBasedVersion = 1
  _Version = 1
FEATURE [Sketcher::SketchObject] Sketch127
  ArcFitTolerance = 0
  AttachmentSupport = -> [XZ_Plane068]
  ExternalBSplineMaxDegree = 0
  ExternalBSplineTolerance = 0
  FullyConstrained = true
  InternalTolerance = 1e-06
  MakeInternals = false
  MapMode = 5
  Placement = pos=(0,0,0) rot=(1,0,0;1.5708rad)
  Support = -> [XZ_Plane068]
  TreeRank = 0
  sketch-geometry (1):
    g0: Circle CenterX=0 CenterY=0 CenterZ=0 NormalX=0 NormalY=0 NormalZ=1 AngleXU=0 Radius=3.75
  constraints (2):
    c: Coincident(g0,g-1)
    c: Diameter(g0) = 7.5
FEATURE [PartDesign::Pocket] Pocket051
  AddSubType = 1
  AutoTaperInnerAngle = false
  BaseFeature = -> Pocket050
  CheckUpToFaceLimits = true
  ClaimChildren = false
  Fit = 0
  FitJoin = 0
  InnerFit = 0
  InnerFitJoin = 0
  Length = 4
  Length2 = 100
  Linearize = true
  NewSolid = false
  Placement = pos=(0,0,0) rot=(1,0,0;1.5708rad)
  Profile = -> Sketch127
  Refine = true
  Suppress = false
  TaperInnerAngle = 0
  TaperInnerAngleRev = 0
  TreeRank = 0
  Type = 0
  _ProfileBasedVersion = 1
  _Version = 1
FEATURE [PartDesign::Chamfer] Chamfer040
  AddSubType = 0
  Angle = 45
  Base = -> Pocket051 [Edge24,Edge14]
  BaseFeature = -> Pocket051
  ChamferType = 0
  FlipDirection = false
  NewSolid = false
  Placement = pos=(0,0,0) rot=(1,0,0;1.5708rad)
  Refine = true
  Size = 0.2
  Size2 = 1
  SupportTransform = false
  Suppress = false
  TreeRank = 0
FEATURE [PartDesign::Chamfer] Chamfer041
  AddSubType = 0
  Angle = 45
  Base = -> Chamfer040 [Edge25]
  BaseFeature = -> Chamfer040
  ChamferType = 0
  FlipDirection = false
  NewSolid = false
  Placement = pos=(0,0,0) rot=(1,0,0;1.5708rad)
  Refine = true
  Size = 0.2
  Size2 = 1
  SupportTransform = false
  Suppress = false
  TreeRank = 0
FEATURE [PartDesign::Body] Body057  label="PalonnierElastique"
  AutoGroupSolids = false
  ClaimAllChildren = false
  ExportMode = 0
  Group = -> [Sketch123,Pad066,Sketch124,Pad067,Sketch125,Pocket049,Sketch126,Pocket050,Sketch127,Pocket051,Chamfer040,Chamfer041]
  Origin = -> Origin085
  Placement = pos=(-1.09497e-05,-4.80001,-1.51983e-05) rot=(0,1,0;1.5708rad)
  SingleSolid = true
  Tip = -> Chamfer041
  TreeRank = 0
  _ExportChildren = -> [Pad066,Pad067,Pocket049,Pocket050,Pocket051,Chamfer040,Chamfer041]
  _GroupVersion = 1
COMPONENT P7 — recipe-attached ("Ventouse20mm", modeled in this document).
Construction recipe (the document's own serialized feature program — sketch geometry with constraints, then the solid features built on it; lengths are millimeters unless a unit is written):

FEATURE [Sketcher::SketchObject] Sketch136
  ArcFitTolerance = 0
  AttachmentSupport = -> [XZ_Plane076]
  ExternalBSplineMaxDegree = 0
  ExternalBSplineTolerance = 0
  FullyConstrained = true
  InternalTolerance = 1e-06
  MakeInternals = false
  MapMode = 5
  Placement = pos=(0,0,0) rot=(1,0,0;1.5708rad)
  Support = -> [XZ_Plane076]
  TreeRank = 0
  sketch-geometry (15):
    g0: LineSegment [constr] StartX=0 StartY=0 StartZ=0 EndX=0 EndY=8 EndZ=0
    g1: LineSegment StartX=0 StartY=8 StartZ=0 EndX=-7 EndY=8 EndZ=0
    g2: LineSegment StartX=-7 StartY=8 StartZ=0 EndX=-8.57143 EndY=6 EndZ=0
    g3: LineSegment StartX=-8.57143 StartY=6 StartZ=0 EndX=-11.7143 EndY=10 EndZ=0
    g4: LineSegment StartX=-11.7143 StartY=10 StartZ=0 EndX=-14.8571 EndY=6 EndZ=0
    g5: LineSegment StartX=-14.8571 StartY=6 StartZ=0 EndX=-18 EndY=10 EndZ=0
    g6: LineSegment [constr] StartX=-18 StartY=10 StartZ=0 EndX=-18 EndY=0 EndZ=0
    g7: LineSegment [constr] StartX=-18 StartY=0 StartZ=0 EndX=0 EndY=0 EndZ=0
    g8: LineSegment [constr] StartX=-8.57143 StartY=6 StartZ=0 EndX=-5.42857 EndY=10 EndZ=0
    g9: LineSegment StartX=-15 StartY=4.5 StartZ=0 EndX=-6 EndY=4.5 EndZ=0
    g10: LineSegment StartX=-6 StartY=4.5 StartZ=0 EndX=-6 EndY=2.5 EndZ=0
    g11: LineSegment StartX=-6 StartY=2.5 StartZ=0 EndX=0 EndY=2.5 EndZ=0
    g12: LineSegment StartX=0 StartY=2.5 StartZ=0 EndX=0 EndY=8 EndZ=0
    g13: LineSegment StartX=-18 StartY=10 StartZ=0 EndX=-18 EndY=9.6 EndZ=0
    g14: LineSegment StartX=-15 StartY=4.5 StartZ=0 EndX=-18 EndY=9.6 EndZ=0
  constraints (43):
    c: Coincident(g-1,g0)
    c: PointOnObject(g0,g-2)
    c: Coincident(g0,g1)
    c: Horizontal(g1)
    c: Coincident(g1,g2)
    c: Coincident(g2,g3)
    c: Coincident(g3,g4)
    c: Coincident(g4,g5)
    c: Coincident(g5,g6)
    c: Vertical(g6)
    c: Coincident(g6,g7)
    c: Coincident(g7,g0)
    c: Horizontal(g7)
    c: DistanceY(g0) = 8
    c: DistanceY(g5) = 10
    c: DistanceY(g3) = 10
    c: DistanceX(g5) = -18
    c: Equal(g3,g4)
    c: DistanceY(g2) = 6
    c: Horizontal(g4,g2)
    c: Equal(g4,g5)
    c: DistanceX(g1,g1) = 7
    c: Coincident(g8,g2)
    c: PointOnObject(g1,g8)
    c: Equal(g8,g3)
    c: Horizontal(g8,g3)
    c: Horizontal(g9)
    c: Coincident(g9,g10)
    c: Vertical(g10)
    c: Coincident(g10,g11)
    c: PointOnObject(g11,g0)
    c: Horizontal(g11)
    c: Coincident(g12,g11)
    c: Coincident(g12,g1)
    c: DistanceY(g11) = 2.5
    c: DistanceX(g11,g11) = 6
    c: DistanceY(g9) = 4.5
    c: Coincident(g13,g5)
    c: PointOnObject(g13,g6)
    c: Coincident(g14,g9)
    c: Coincident(g14,g13)
    c: DistanceY(g13,g5) = 0.4
    c: DistanceX(g9,g9) = 9
FEATURE [PartDesign::Revolution] Revolution009
  AddSubType = 0
  Angle = 360
  Axis = (1,0,0)
  Base = (0,0,0)
  ClaimChildren = false
  Fit = 0
  FitJoin = 0
  InnerFit = 0
  InnerFitJoin = 0
  NewSolid = false
  Placement = pos=(0,0,0) rot=(1,0,0;1.5708rad)
  Profile = -> Sketch136
  ReferenceAxis = -> Sketch136 [H_Axis]
  Refine = true
  Suppress = false
  TreeRank = 0
  _ProfileBasedVersion = 1
FEATURE [PartDesign::Fillet] Fillet040
  AddSubType = 0
  Base = -> Revolution009 [Edge7,Edge8]
  BaseFeature = -> Revolution009
  NewSolid = false
  Placement = pos=(0,0,0) rot=(1,0,0;1.5708rad)
  Radius = 0.4
  Refine = true
  SupportTransform = false
  Suppress = false
  TreeRank = 0
FEATURE [PartDesign::Body] Body063  label="Ventouse20mm"
  AutoGroupSolids = false
  ClaimAllChildren = false
  ExportMode = 0
  Group = -> [Sketch136,Revolution009,Fillet040]
  Origin = -> Origin098
  SingleSolid = true
  Tip = -> Fillet040
  TreeRank = 160
  _ExportChildren = -> [Revolution009,Fillet040]
  _GroupVersion = 1
COMPONENT P8 — recipe-attached ("MB_150", modeled in this document).
Construction recipe (the document's own serialized feature program — sketch geometry with constraints, then the solid features built on it; lengths are millimeters unless a unit is written):

FEATURE [Sketcher::SketchObject] Sketch200
  ArcFitTolerance = 0
  AttachmentSupport = -> [XZ_Plane115]
  ExternalBSplineMaxDegree = 0
  ExternalBSplineTolerance = 0
  FullyConstrained = true
  InternalTolerance = 1e-06
  MakeInternals = false
  MapMode = 5
  Placement = pos=(0,0,0) rot=(1,0,0;1.5708rad)
  Support = -> [XZ_Plane115]
  TreeRank = 0
  sketch-geometry (14):
    g0: ArcOfCircle CenterX=0 CenterY=0 CenterZ=0 NormalX=0 NormalY=0 NormalZ=1 AngleXU=0 Radius=1.25 StartAngle=0 EndAngle=1.5708
    g1: LineSegment StartX=1e-16 StartY=1.25 StartZ=0 EndX=0 EndY=2 EndZ=0
    g2: LineSegment StartX=0 StartY=2 StartZ=0 EndX=1 EndY=2 EndZ=0
    g3: LineSegment [constr] StartX=0 StartY=0 StartZ=0 EndX=5 EndY=5 EndZ=0
    g4: LineSegment StartX=1 StartY=2 StartZ=0 EndX=3.3 EndY=4 EndZ=0
    g5: LineSegment StartX=3.3 StartY=4 StartZ=0 EndX=1.5 EndY=4 EndZ=0
    g6: LineSegment StartX=1.5 StartY=4 StartZ=0 EndX=1.5 EndY=5 EndZ=0
    g7: LineSegment StartX=1.5 StartY=5 StartZ=0 EndX=5 EndY=5 EndZ=0
    g8: LineSegment StartX=5 StartY=5 StartZ=0 EndX=5 EndY=1.5 EndZ=0
    g9: LineSegment StartX=5 StartY=1.5 StartZ=0 EndX=4 EndY=1.5 EndZ=0
    g10: LineSegment StartX=4 StartY=1.5 StartZ=0 EndX=4 EndY=3.3 EndZ=0
    g11: LineSegment StartX=4 StartY=3.3 StartZ=0 EndX=2 EndY=1 EndZ=0
    g12: LineSegment StartX=2 StartY=1 StartZ=0 EndX=2 EndY=0 EndZ=0
    g13: LineSegment StartX=2 StartY=0 StartZ=0 EndX=1.25 EndY=0 EndZ=0
  constraints (41):
    c: Coincident(g0,g-1)
    c: PointOnObject(g0,g-1)
    c: PointOnObject(g0,g-2)
    c: Coincident(g1,g0)
    c: PointOnObject(g1,g-2)
    c: Coincident(g2,g1)
    c: Horizontal(g2)
    c: Coincident(g3,g0)
    c: Angle(g-1,g3) = 0.785398
    c: DistanceX(g3) = 5
    c: Diameter(g0) = 2.5
    c: DistanceX(g2) = 1
    c: Coincident(g4,g2)
    c: Coincident(g5,g4)
    c: Horizontal(g5)
    c: Coincident(g6,g5)
    c: Vertical(g6)
    c: Coincident(g7,g6)
    c: Coincident(g7,g3)
    c: Coincident(g8,g7)
    c: Vertical(g8)
    c: Coincident(g9,g8)
    c: Coincident(g10,g9)
    c: Vertical(g10)
    c: Coincident(g11,g10)
    c: Coincident(g12,g11)
    c: PointOnObject(g12,g-1)
    c: Vertical(g12)
    c: Coincident(g13,g12)
    c: Coincident(g13,g0)
    c: Equal(g12,g2)
    c: Equal(g13,g1)
    c: Horizontal(g7)
    c: Horizontal(g9)
    c: Equal(g6,g9)
    c: Equal(g11,g4)
    c: Equal(g5,g10)
    c: DistanceY(g2,g6) = 3
    c: DistanceX(g6) = 1.5
    c: DistanceY(g6,g6) = 1
    c: DistanceX(g5,g5) = 1.8
FEATURE [PartDesign::Pad] Pad081
  AddSubType = 0
  AlongSketchNormal = false
  AutoTaperInnerAngle = false
  CheckUpToFaceLimits = true
  ClaimChildren = false
  Direction = (0,-1,-2e-16)
  Fit = 0
  FitJoin = 0
  InnerFit = 0
  InnerFitJoin = 0
  Length = 150
  Length2 = 100
  NewSolid = false
  Profile = -> Sketch200
  Refine = true
  Reversed = true
  Suppress = false
  TaperInnerAngle = 0
  TaperInnerAngleRev = 0
  TreeRank = 0
  Type = 0
  _ProfileBasedVersion = 0
FEATURE [PartDesign::PolarPattern] PolarPattern013
  AddSubType = 0
  Angle = 360
  Axis = -> Y_Axis115
  BaseFeature = -> Pad081
  CopyShape = false
  NewSolid = false
  Occurrences = 4
  OriginalSubs = -> [Pad081]
  Originals = -> [Pad081]
  ParallelTransform = true
  Refine = true
  SubTransform = true
  Suppress = false
  TreeRank = 0
  _Version = 0
FEATURE [PartDesign::CoordinateSystem] Local_CS003
  AttacherType = Attacher::AttachEngine3D
  AttachmentSupport = -> [PolarPattern013]
  MapMode = 11
  Placement = pos=(3.33e-14,150,-6.66e-14) rot=(0.57735,0.57735,-0.57735;2.0944rad)
  Support = -> [PolarPattern013]
  TreeRank = 0
FEATURE [PartDesign::Body] Body095  label="MB_150"
  AutoGroupSolids = false
  ClaimAllChildren = false
  ExportMode = 0
  Group = -> [Sketch200,Pad081,PolarPattern013,Local_CS003]
  Origin = -> Origin185
  SingleSolid = true
  Tip = -> PolarPattern013
  TreeRank = 315
  _ExportChildren = -> [Pad081,PolarPattern013,Local_CS003]
  _GroupVersion = 1
COMPONENT P9 — recipe-attached ("MB_200", modeled in this document).
Construction recipe (the document's own serialized feature program — sketch geometry with constraints, then the solid features built on it; lengths are millimeters unless a unit is written):

FEATURE [Sketcher::SketchObject] Sketch201
  ArcFitTolerance = 0
  AttachmentSupport = -> [XZ_Plane116]
  ExternalBSplineMaxDegree = 0
  ExternalBSplineTolerance = 0
  FullyConstrained = true
  InternalTolerance = 1e-06
  MakeInternals = false
  MapMode = 5
  Placement = pos=(0,0,0) rot=(1,0,0;1.5708rad)
  Support = -> [XZ_Plane116]
  TreeRank = 0
  sketch-geometry (14):
    g0: ArcOfCircle CenterX=0 CenterY=0 CenterZ=0 NormalX=0 NormalY=0 NormalZ=1 AngleXU=0 Radius=1.25 StartAngle=0 EndAngle=1.5708
    g1: LineSegment StartX=1e-16 StartY=1.25 StartZ=0 EndX=0 EndY=2 EndZ=0
    g2: LineSegment StartX=0 StartY=2 StartZ=0 EndX=1 EndY=2 EndZ=0
    g3: LineSegment [constr] StartX=0 StartY=0 StartZ=0 EndX=5 EndY=5 EndZ=0
    g4: LineSegment StartX=1 StartY=2 StartZ=0 EndX=3.3 EndY=4 EndZ=0
    g5: LineSegment StartX=3.3 StartY=4 StartZ=0 EndX=1.5 EndY=4 EndZ=0
    g6: LineSegment StartX=1.5 StartY=4 StartZ=0 EndX=1.5 EndY=5 EndZ=0
    g7: LineSegment StartX=1.5 StartY=5 StartZ=0 EndX=5 EndY=5 EndZ=0
    g8: LineSegment StartX=5 StartY=5 StartZ=0 EndX=5 EndY=1.5 EndZ=0
    g9: LineSegment StartX=5 StartY=1.5 StartZ=0 EndX=4 EndY=1.5 EndZ=0
    g10: LineSegment StartX=4 StartY=1.5 StartZ=0 EndX=4 EndY=3.3 EndZ=0
    g11: LineSegment StartX=4 StartY=3.3 StartZ=0 EndX=2 EndY=1 EndZ=0
    g12: LineSegment StartX=2 StartY=1 StartZ=0 EndX=2 EndY=0 EndZ=0
    g13: LineSegment StartX=2 StartY=0 StartZ=0 EndX=1.25 EndY=0 EndZ=0
  constraints (41):
    c: Coincident(g0,g-1)
    c: PointOnObject(g0,g-1)
    c: PointOnObject(g0,g-2)
    c: Coincident(g1,g0)
    c: PointOnObject(g1,g-2)
    c: Coincident(g2,g1)
    c: Horizontal(g2)
    c: Coincident(g3,g0)
    c: Angle(g-1,g3) = 0.785398
    c: DistanceX(g3) = 5
    c: Diameter(g0) = 2.5
    c: DistanceX(g2) = 1
    c: Coincident(g4,g2)
    c: Coincident(g5,g4)
    c: Horizontal(g5)
    c: Coincident(g6,g5)
    c: Vertical(g6)
    c: Coincident(g7,g6)
    c: Coincident(g7,g3)
    c: Coincident(g8,g7)
    c: Vertical(g8)
    c: Coincident(g9,g8)
    c: Coincident(g10,g9)
    c: Vertical(g10)
    c: Coincident(g11,g10)
    c: Coincident(g12,g11)
    c: PointOnObject(g12,g-1)
    c: Vertical(g12)
    c: Coincident(g13,g12)
    c: Coincident(g13,g0)
    c: Equal(g12,g2)
    c: Equal(g13,g1)
    c: Horizontal(g7)
    c: Horizontal(g9)
    c: Equal(g6,g9)
    c: Equal(g11,g4)
    c: Equal(g5,g10)
    c: DistanceY(g2,g6) = 3
    c: DistanceX(g6) = 1.5
    c: DistanceY(g6,g6) = 1
    c: DistanceX(g5,g5) = 1.8
FEATURE [PartDesign::Pad] Pad082
  AddSubType = 0
  AlongSketchNormal = false
  AutoTaperInnerAngle = false
  CheckUpToFaceLimits = true
  ClaimChildren = false
  Direction = (0,-1,-2e-16)
  Fit = 0
  FitJoin = 0
  InnerFit = 0
  InnerFitJoin = 0
  Length = 200
  Length2 = 100
  NewSolid = false
  Profile = -> Sketch201
  Refine = true
  Reversed = true
  Suppress = false
  TaperInnerAngle = 0
  TaperInnerAngleRev = 0
  TreeRank = 0
  Type = 0
  _ProfileBasedVersion = 0
FEATURE [PartDesign::PolarPattern] PolarPattern014
  AddSubType = 0
  Angle = 360
  Axis = -> Y_Axis116
  BaseFeature = -> Pad082
  CopyShape = false
  NewSolid = false
  Occurrences = 4
  OriginalSubs = -> [Pad082]
  Originals = -> [Pad082]
  ParallelTransform = true
  Refine = true
  SubTransform = true
  Suppress = false
  TreeRank = 0
  _Version = 0
FEATURE [PartDesign::CoordinateSystem] Local_CS004
  AttacherType = Attacher::AttachEngine3D
  AttachmentSupport = -> [PolarPattern014]
  MapMode = 11
  Placement = pos=(4.44e-14,200,-8.88e-14) rot=(0.57735,0.57735,-0.57735;2.0944rad)
  Support = -> [PolarPattern014]
  TreeRank = 0
FEATURE [PartDesign::Body] Body096  label="MB_200"
  AutoGroupSolids = false
  ClaimAllChildren = false
  ExportMode = 0
  Group = -> [Sketch201,Pad082,PolarPattern014,Local_CS004]
  Origin = -> Origin186
  SingleSolid = true
  Tip = -> PolarPattern014
  TreeRank = 316
  _ExportChildren = -> [Pad082,PolarPattern014,Local_CS004]
  _GroupVersion = 1
COMPONENT P10 — geometry summary ("MB1r2t"; no construction recipe available for this part):
  bounding box: 98.6 x 87.0 x 64.0 mm
  tessellated surface: 127,664 triangles
  volume: 120319 mm^3 (22% of its bounding box)
COMPONENT P11 — recipe-attached ("Link(ServoMG996R001)", modeled in this document).
Construction recipe (the document's own serialized feature program — sketch geometry with constraints, then the solid features built on it; lengths are millimeters unless a unit is written):

FEATURE [Sketcher::SketchObject] Sketch086
  ArcFitTolerance = 0
  AttachmentSupport = -> [XZ_Plane049]
  ExternalBSplineMaxDegree = 0
  ExternalBSplineTolerance = 0
  FullyConstrained = true
  InternalTolerance = 1e-06
  MakeInternals = false
  MapMode = 5
  Placement = pos=(0,0,0) rot=(1,0,0;1.5708rad)
  Support = -> [XZ_Plane049]
  TreeRank = 0
  sketch-geometry (12):
    g0: LineSegment StartX=-37 StartY=-18.5 StartZ=0 EndX=-37 EndY=-16 EndZ=0
    g1: LineSegment StartX=-37 StartY=-16 StartZ=0 EndX=-30 EndY=-16 EndZ=0
    g2: LineSegment StartX=-30 StartY=-16 StartZ=0 EndX=-30 EndY=-8 EndZ=0
    g3: LineSegment StartX=-30 StartY=-8 StartZ=0 EndX=10 EndY=-8 EndZ=0
    g4: LineSegment StartX=10 StartY=-8 StartZ=0 EndX=10 EndY=-16 EndZ=0
    g5: LineSegment StartX=10 StartY=-16 StartZ=0 EndX=17 EndY=-16 EndZ=0
    g6: LineSegment StartX=17 StartY=-16 StartZ=0 EndX=17 EndY=-18.5 EndZ=0
    g7: LineSegment StartX=17 StartY=-18.5 StartZ=0 EndX=10 EndY=-18.5 EndZ=0
    g8: LineSegment StartX=10 StartY=-18.5 StartZ=0 EndX=10 EndY=-47 EndZ=0
    g9: LineSegment StartX=10 StartY=-47 StartZ=0 EndX=-30 EndY=-47 EndZ=0
    g10: LineSegment StartX=-30 StartY=-47 StartZ=0 EndX=-30 EndY=-18.5 EndZ=0
    g11: LineSegment StartX=-30 StartY=-18.5 StartZ=0 EndX=-37 EndY=-18.5 EndZ=0
  constraints (33):
    c: Vertical(g0)
    c: Coincident(g0,g1)
    c: Horizontal(g1)
    c: Coincident(g1,g2)
    c: Vertical(g2)
    c: Coincident(g2,g3)
    c: Horizontal(g3)
    c: Coincident(g3,g4)
    c: Coincident(g4,g5)
    c: Coincident(g5,g6)
    c: Vertical(g6)
    c: Coincident(g6,g7)
    c: Horizontal(g7)
    c: Coincident(g7,g8)
    c: Vertical(g8)
    c: Coincident(g8,g9)
    c: Horizontal(g9)
    c: Coincident(g9,g10)
    c: Coincident(g10,g11)
    c: Coincident(g11,g0)
    c: Horizontal(g11)
    c: Tangent(g4,g8) = -1.5708
    c: Tangent(g10,g2)
    c: Equal(g1,g5)
    c: Tangent(g1,g5)
    c: Equal(g6,g0)
    c: DistanceX(g-1,g3) = 10
    c: DistanceX(g0,g5) = 54
    c: DistanceX(g10,g7) = 40
    c: DistanceY(g9,g-1) = 47
    c: DistanceY(g3,g-1) = 8
    c: DistanceY(g6,g6) = 2.5
    c: DistanceY(g0,g-1) = 18.5
FEATURE [PartDesign::Pad] Pad050
  AddSubType = 0
  AutoTaperInnerAngle = false
  CheckUpToFaceLimits = true
  ClaimChildren = false
  Direction = (1,1,1)
  Fit = 0
  FitJoin = 0
  InnerFit = 0
  InnerFitJoin = 0
  Length = 20
  Length2 = 100
  Linearize = true
  Midplane = true
  NewSolid = false
  Placement = pos=(0,0,0) rot=(1,0,0;1.5708rad)
  Profile = -> Sketch086
  Refine = true
  Suppress = false
  TaperInnerAngle = 0
  TaperInnerAngleRev = 0
  TreeRank = 0
  Type = 0
  _ProfileBasedVersion = 1
FEATURE [Sketcher::SketchObject] Sketch087
  ArcFitTolerance = 0
  AttachmentSupport = -> [XY_Plane049]
  ExternalBSplineMaxDegree = 0
  ExternalBSplineTolerance = 0
  FullyConstrained = true
  InternalTolerance = 1e-06
  MakeInternals = false
  MapMode = 5
  Support = -> [XY_Plane049]
  TreeRank = 0
  sketch-geometry (4):
    g0: Circle CenterX=14.5 CenterY=5 CenterZ=0 NormalX=0 NormalY=0 NormalZ=1 AngleXU=0 Radius=2
    g1: Circle CenterX=14.5 CenterY=-5 CenterZ=0 NormalX=0 NormalY=0 NormalZ=1 AngleXU=0 Radius=2
    g2: Circle CenterX=-34.5 CenterY=5 CenterZ=0 NormalX=0 NormalY=0 NormalZ=1 AngleXU=0 Radius=2
    g3: Circle CenterX=-34.5 CenterY=-5 CenterZ=0 NormalX=0 NormalY=0 NormalZ=1 AngleXU=0 Radius=2
  constraints (10):
    c: Equal(g2,g3)
    c: Equal(g3,g1)
    c: Equal(g1,g0)
    c: Symmetric(g0,g1,g-1)
    c: Symmetric(g2,g3,g-1)
    c: Horizontal(g2,g0)
    c: Diameter(g0) = 4
    c: DistanceY(g1,g0) = 10
    c: DistanceX(g2,g0) = 49
    c: DistanceX(g-1,g0) = 14.5
FEATURE [PartDesign::Pocket] Pocket033
  AddSubType = 1
  AutoTaperInnerAngle = false
  BaseFeature = -> Pad050
  CheckUpToFaceLimits = true
  ClaimChildren = false
  Fit = 0
  FitJoin = 0
  InnerFit = 0
  InnerFitJoin = 0
  Length = 5
  Length2 = 100
  Linearize = true
  NewSolid = false
  Placement = pos=(0,0,0) rot=(1,0,0;1.5708rad)
  Profile = -> Sketch087
  Refine = true
  Suppress = false
  TaperInnerAngle = 0
  TaperInnerAngleRev = 0
  TreeRank = 0
  Type = 1
  _ProfileBasedVersion = 1
  _Version = 0
FEATURE [PartDesign::Fillet] Fillet024
  AddSubType = 0
  Base = -> Pocket033 [Edge28,Edge19,Edge4,Edge3]
  BaseFeature = -> Pocket033
  NewSolid = false
  Placement = pos=(0,0,0) rot=(1,0,0;1.5708rad)
  Radius = 1
  Refine = true
  SupportTransform = false
  Suppress = false
  TreeRank = 0
FEATURE [PartDesign::Body] Body041  label="ServoBody001"
  AutoGroupSolids = false
  ClaimAllChildren = false
  ExportMode = 0
  Group = -> [Sketch086,Pad050,Sketch087,Pocket033,Fillet024]
  Origin = -> Origin062
  SingleSolid = true
  Tip = -> Fillet024
  TreeRank = 0
  _ExportChildren = -> [Pad050,Pocket033,Fillet024]
  _GroupVersion = 1
FEATURE [Sketcher::SketchObject] Sketch090
  ArcFitTolerance = 0
  AttachmentOffset = pos=(0,0,-2) rot=(0,0,1;0rad)
  AttachmentSupport = -> [XY_Plane051]
  ExternalBSplineMaxDegree = 0
  ExternalBSplineTolerance = 0
  FullyConstrained = true
  InternalTolerance = 1e-06
  MakeInternals = false
  MapMode = 5
  Placement = pos=(0,0,-2) rot=(0,0,1;0rad)
  Support = -> [XY_Plane051]
  TreeRank = 0
  sketch-geometry (1):
    g0: Circle CenterX=0 CenterY=0 CenterZ=0 NormalX=0 NormalY=0 NormalZ=1 AngleXU=0 Radius=3
  constraints (2):
    c: Coincident(g0,g-1)
    c: Diameter(g0) = 6
FEATURE [PartDesign::Pad] Pad053
  AddSubType = 0
  AutoTaperInnerAngle = false
  CheckUpToFaceLimits = true
  ClaimChildren = false
  Direction = (1,1,1)
  Fit = 0
  FitJoin = 0
  InnerFit = 0
  InnerFitJoin = 0
  Length = 10
  Length2 = 100
  Linearize = true
  NewSolid = false
  Profile = -> Sketch090
  Refine = true
  Reversed = true
  Suppress = false
  TaperInnerAngle = 0
  TaperInnerAngleRev = 0
  TreeRank = 0
  Type = 0
  _ProfileBasedVersion = 1
FEATURE [PartDesign::Chamfer] Chamfer029
  AddSubType = 0
  Angle = 45
  Base = -> Pad053 [Edge2]
  BaseFeature = -> Pad053
  ChamferType = 0
  FlipDirection = false
  NewSolid = false
  Refine = true
  Size = 0.5
  Size2 = 1
  SupportTransform = false
  Suppress = false
  TreeRank = 0
FEATURE [PartDesign::Body] Body043  label="ServoAxis001"
  AutoGroupSolids = false
  ClaimAllChildren = false
  ExportMode = 0
  Group = -> [Sketch090,Pad053,Chamfer029]
  Origin = -> Origin064
  SingleSolid = true
  Tip = -> Chamfer029
  TreeRank = 0
  _ExportChildren = -> [Pad053,Chamfer029]
  _GroupVersion = 1
COMPONENT P12 — recipe-attached ("ServoMG-SG90", modeled in this document).
Construction recipe (the document's own serialized feature program — sketch geometry with constraints, then the solid features built on it; lengths are millimeters unless a unit is written):

FEATURE [Sketcher::SketchObject] Sketch162
  ArcFitTolerance = 0
  AttachmentSupport = -> [XY_Plane096]
  ExternalBSplineMaxDegree = 0
  ExternalBSplineTolerance = 0
  FullyConstrained = true
  InternalTolerance = 1e-06
  MakeInternals = false
  MapMode = 5
  Support = -> [XY_Plane096]
  TreeRank = 36
  sketch-geometry (12):
    g0: LineSegment StartX=-17 StartY=2.106e-12 StartZ=0 EndX=-21.7 EndY=5.127e-13 EndZ=0
    g1: LineSegment StartX=-21.7 StartY=5.127e-13 StartZ=0 EndX=-21.7 EndY=-2.4 EndZ=0
    g2: LineSegment StartX=-21.7 StartY=-2.4 StartZ=0 EndX=-17 EndY=-2.4 EndZ=0
    g3: LineSegment StartX=-17 StartY=-2.4 StartZ=0 EndX=-17 EndY=-6.8 EndZ=0
    g4: LineSegment StartX=-17 StartY=-6.8 StartZ=0 EndX=6 EndY=-6.8 EndZ=0
    g5: LineSegment StartX=6 StartY=-6.8 StartZ=0 EndX=6 EndY=-2.4 EndZ=0
    g6: LineSegment StartX=6 StartY=-2.4 StartZ=0 EndX=10.7 EndY=-2.4 EndZ=0
    g7: LineSegment StartX=10.7 StartY=-2.4 StartZ=0 EndX=10.7 EndY=1.124e-12 EndZ=0
    g8: LineSegment StartX=10.7 StartY=1.1239e-12 StartZ=0 EndX=6 EndY=-1.9734e-12 EndZ=0
    g9: LineSegment StartX=6 StartY=-1.9734e-12 StartZ=0 EndX=6 EndY=15.8 EndZ=0
    g10: LineSegment StartX=6 StartY=15.8 StartZ=0 EndX=-17 EndY=15.8 EndZ=0
    g11: LineSegment StartX=-17 StartY=15.8 StartZ=0 EndX=-17 EndY=2.1068e-12 EndZ=0
  constraints (36):
    c: PointOnObject(g0,g-1)
    c: PointOnObject(g0,g-1)
    c: Coincident(g0,g1)
    c: Vertical(g1)
    c: Coincident(g1,g2)
    c: Horizontal(g2)
    c: Coincident(g2,g3)
    c: Vertical(g3)
    c: Coincident(g3,g4)
    c: Horizontal(g4)
    c: Coincident(g4,g5)
    c: Vertical(g5)
    c: Coincident(g5,g6)
    c: Horizontal(g6)
    c: Coincident(g6,g7)
    c: PointOnObject(g7,g-1)
    c: Vertical(g7)
    c: Coincident(g7,g8)
    c: PointOnObject(g8,g-1)
    c: Coincident(g8,g9)
    c: Vertical(g9)
    c: Coincident(g9,g10)
    c: Horizontal(g10)
    c: Coincident(g10,g11)
    c: Coincident(g11,g0)
    c: Vertical(g11)
    c: Equal(g0,g2)
    c: Equal(g2,g6)
    c: Equal(g6,g8)
    c: DistanceX(g4) = 6
    c: DistanceX(g4,g4) = 23
    c: DistanceX(g1,g6) = 32.4
    c: DistanceY(g3,g3) = 4.4
    c: DistanceY(g1,g1) = 2.4
    c: Equal(g7,g1)
    c: DistanceY(g9,g9) = 15.8
FEATURE [PartDesign::Pad] Pad068
  AddSubType = 0
  AlongSketchNormal = false
  AutoTaperInnerAngle = false
  CheckUpToFaceLimits = true
  ClaimChildren = false
  Direction = (0,0,1)
  Fit = 0
  FitJoin = 0
  InnerFit = 0
  InnerFitJoin = 0
  Length = 12
  Length2 = 100
  Linearize = true
  Midplane = true
  NewSolid = false
  Profile = -> Sketch162
  Refine = true
  Suppress = false
  TaperInnerAngle = 0
  TaperInnerAngleRev = 0
  TreeRank = 37
  Type = 0
  _ProfileBasedVersion = 1
FEATURE [Sketcher::SketchObject] Sketch163
  ArcFitTolerance = 0
  AttachmentSupport = -> [Pad068]
  ExternalBSplineMaxDegree = 0
  ExternalBSplineTolerance = 0
  FullyConstrained = true
  InternalTolerance = 1e-06
  MakeInternals = false
  MapMode = 5
  Placement = pos=(0,-6.8,0) rot=(1,0,0;1.5708rad)
  Support = -> [Pad068]
  TreeRank = 38
  sketch-geometry (4):
    g0: ArcOfCircle CenterX=-5.554e-13 CenterY=-7.838e-13 CenterZ=0 NormalX=0 NormalY=0 NormalZ=1 AngleXU=0 Radius=6 StartAngle=3.57137 EndAngle=8.995
    g1: ArcOfCircle CenterX=-6 CenterY=4.736e-13 CenterZ=0 NormalX=0 NormalY=0 NormalZ=1 AngleXU=0 Radius=2.5 StartAngle=1.5708 EndAngle=4.71239
    g2: LineSegment StartX=-6 StartY=2.5 StartZ=0 EndX=-5.45436 EndY=2.5 EndZ=0
    g3: LineSegment StartX=-6 StartY=-2.5 StartZ=0 EndX=-5.45436 EndY=-2.5 EndZ=0
  constraints (11):
    c: Coincident(g0,g-1)
    c: PointOnObject(g1,g-1)
    c: Coincident(g2,g0)
    c: Coincident(g3,g0)
    c: Horizontal(g3)
    c: Horizontal(g2)
    c: Tangent(g2,g1) = 1.5708
    c: Tangent(g3,g1) = -1.5708
    c: Radius(g0) = 6
    c: DistanceY(g1,g1) = 5
    c: DistanceX(g1,g0) = 6
FEATURE [PartDesign::Pad] Pad069
  AddSubType = 0
  AlongSketchNormal = false
  AutoTaperInnerAngle = false
  BaseFeature = -> Pad068
  CheckUpToFaceLimits = true
  ClaimChildren = false
  Direction = (0,-1,2e-16)
  Fit = 0
  FitJoin = 0
  InnerFit = 0
  InnerFitJoin = 0
  Length = 4
  Length2 = 100
  Linearize = true
  NewSolid = false
  Profile = -> Sketch163
  Refine = true
  Suppress = false
  TaperInnerAngle = 0
  TaperInnerAngleRev = 0
  TreeRank = 39
  Type = 0
  _ProfileBasedVersion = 1
FEATURE [Sketcher::SketchObject] Sketch164
  ArcFitTolerance = 0
  AttachmentSupport = -> [XZ_Plane096]
  ExternalBSplineMaxDegree = 0
  ExternalBSplineTolerance = 0
  ExternalGeometry = -> [Pad069]
  FullyConstrained = true
  InternalTolerance = 1e-06
  MakeInternals = false
  MapMode = 5
  Placement = pos=(0,0,0) rot=(1,0,0;1.5708rad)
  Support = -> [XZ_Plane096]
  TreeRank = 40
  sketch-geometry (4):
    g0: Circle CenterX=-19.25 CenterY=-8.88e-14 CenterZ=0 NormalX=0 NormalY=0 NormalZ=1 AngleXU=0 Radius=1
    g1: Circle CenterX=8.25 CenterY=8.765e-12 CenterZ=0 NormalX=0 NormalY=0 NormalZ=1 AngleXU=0 Radius=1
    g2: LineSegment [constr] StartX=-21.7 StartY=-6 StartZ=0 EndX=10.7 EndY=6 EndZ=0
    g3: GeomPoint [constr] X=-5.5 Y=5.2304e-12 Z=0
  constraints (8):
    c: PointOnObject(g0,g-1)
    c: DistanceX(g0,g1) = 27.5
    c: Equal(g0,g1)
    c: Diameter(g0) = 2
    c: Coincident(g2,g-3)
    c: Coincident(g2,g-4)
    c: Symmetric(g-4,g-3,g3)
    c: Symmetric(g0,g1,g3)
FEATURE [PartDesign::Pocket] Pocket052
  AddSubType = 1
  AutoTaperInnerAngle = false
  BaseFeature = -> Pad069
  CheckUpToFaceLimits = true
  ClaimChildren = false
  Fit = 0
  FitJoin = 0
  InnerFit = 0
  InnerFitJoin = 0
  Length = 5
  Length2 = 100
  Linearize = true
  NewSolid = false
  Profile = -> Sketch164
  Refine = true
  Reversed = true
  Suppress = false
  TaperInnerAngle = 0
  TaperInnerAngleRev = 0
  TreeRank = 41
  Type = 1
  _ProfileBasedVersion = 1
  _Version = 1
FEATURE [PartDesign::Body] Body076  label="BodyServo90S"
  AutoGroupSolids = false
  ClaimAllChildren = false
  ExportMode = 0
  Group = -> [Sketch162,Pad068,Sketch163,Pad069,Sketch164,Pocket052]
  Origin = -> Origin
  SingleSolid = true
  Tip = -> Pocket052
  TreeRank = 35
  _ExportChildren = -> [Pad068,Pad069,Pocket052]
  _GroupVersion = 1
FEATURE [Part::SubShapeBinder] Import  label="Import(Pocket052)"
  BindCopyOnChange = 0
  BindMode = 0
  ClaimChildren = false
  Context = -> Group007 [Part.Body077.Import.]
  EdgeTolerance = 1e-06
  FillStyle = 0
  Fuse = false
  MakeFace = false
  MergeEdges = true
  OffsetFill = false
  OffsetIntersection = false
  OffsetJoinType = 0
  OffsetOpenResult = false
  Outline = false
  PartialLoad = false
  Relative = true
  SplitEdges = false
  Support = -> [Body076[Pocket052.]]
  TightBound = false
  TreeRank = 52
  _Version = 8
FEATURE [Sketcher::SketchObject] Sketch165
  ArcFitTolerance = 0
  AttachmentSupport = -> [Import]
  ExternalBSplineMaxDegree = 0
  ExternalBSplineTolerance = 0
  FullyConstrained = true
  InternalTolerance = 1e-06
  MakeInternals = false
  MapMode = 5
  Placement = pos=(0,-10.8,2.3e-15) rot=(1,0,0;1.5708rad)
  Support = -> [Import]
  TreeRank = 53
  sketch-geometry (1):
    g0: Circle CenterX=0 CenterY=0 CenterZ=0 NormalX=0 NormalY=0 NormalZ=1 AngleXU=0 Radius=2.25
  constraints (2):
    c: Coincident(g0,g-1)
    c: Diameter(g0) = 4.5
FEATURE [PartDesign::Pad] Pad070
  AddSubType = 0
  AlongSketchNormal = false
  AutoTaperInnerAngle = false
  CheckUpToFaceLimits = true
  ClaimChildren = false
  Direction = (0,-1,2e-16)
  Fit = 0
  FitJoin = 0
  InnerFit = 0
  InnerFitJoin = 0
  Length = 2.4
  Length2 = 100
  Linearize = true
  NewSolid = false
  Profile = -> Sketch165
  Refine = true
  Suppress = false
  TaperInnerAngle = 0
  TaperInnerAngleRev = 0
  TreeRank = 54
  Type = 0
  _ProfileBasedVersion = 1
FEATURE [PartDesign::Body] Body077  label="AxleServo90S"
  AutoGroupSolids = false
  ClaimAllChildren = false
  ExportMode = 0
  Group = -> [Import,Sketch165,Pad070]
  Origin = -> Origin162
  SingleSolid = true
  Tip = -> Pad070
  TreeRank = 51
  _ExportChildren = -> [Import,Pad070]
  _GroupVersion = 1
FEATURE [Part::SubShapeBinder] Import001  label="Import001(Pocket052)"
  BindCopyOnChange = 0
  BindMode = 0
  ClaimChildren = false
  Context = -> <external ../table_2022.FCStd>#Link005 [Link008.Part031.Link106.Body078.Import001.]
  EdgeTolerance = 1e-06
  FillStyle = 0
  Fuse = false
  MakeFace = false
  MergeEdges = true
  OffsetFill = false
  OffsetIntersection = false
  OffsetJoinType = 0
  OffsetOpenResult = false
  Outline = false
  PartialLoad = false
  Relative = true
  SplitEdges = false
  Support = -> [Body076[Pocket052.]]
  TightBound = false
  TreeRank = 65
  _Version = 8
FEATURE [Sketcher::SketchObject] Sketch166
  ArcFitTolerance = 0
  AttachmentSupport = -> [Import001]
  ExternalBSplineMaxDegree = 0
  ExternalBSplineTolerance = 0
  FullyConstrained = true
  InternalTolerance = 1e-06
  MakeInternals = false
  MapMode = 5
  Placement = pos=(6,0,0) rot=(0.57735,0.57735,0.57735;2.0944rad)
  Support = -> [Import001]
  TreeRank = 74
  sketch-geometry (3):
    g0: Circle CenterX=10 CenterY=-9.4173e-12 CenterZ=0 NormalX=0 NormalY=0 NormalZ=1 AngleXU=0 Radius=0.5
    g1: Circle CenterX=10 CenterY=1 CenterZ=0 NormalX=0 NormalY=0 NormalZ=1 AngleXU=0 Radius=0.5
    g2: Circle CenterX=10 CenterY=-1 CenterZ=0 NormalX=0 NormalY=0 NormalZ=1 AngleXU=0 Radius=0.5
  constraints (9):
    c: PointOnObject(g0,g-1)
    c: Tangent(g1,g0)
    c: Tangent(g2,g0)
    c: Vertical(g2,g0)
    c: Vertical(g0,g1)
    c: Equal(g1,g0)
    c: Equal(g1,g2)
    c: Diameter(g1) = 1
    c: DistanceX(g0) = 10
FEATURE [PartDesign::Pad] Pad071
  AddSubType = 0
  AlongSketchNormal = false
  AutoTaperInnerAngle = false
  CheckUpToFaceLimits = true
  ClaimChildren = false
  Direction = (1,0,0)
  Fit = 0
  FitJoin = 0
  InnerFit = 0
  InnerFitJoin = 0
  Length = 10
  Length2 = 100
  Linearize = true
  NewSolid = false
  Profile = -> Sketch166
  Refine = true
  Suppress = false
  TaperInnerAngle = 0
  TaperInnerAngleRev = 0
  TreeRank = 75
  Type = 0
  _ProfileBasedVersion = 1
FEATURE [PartDesign::Body] Body078  label="Cables001"
  AutoGroupSolids = true
  ClaimAllChildren = false
  ExportMode = 0
  Group = -> [Import001,Sketch166,Pad071]
  Origin = -> Origin163
  Tip = -> Pad071
  TreeRank = 64
  _ExportChildren = -> [Import001,Pad071]
  _GroupVersion = 1
COMPONENT P13 — recipe-attached ("MR148", modeled in this document).
Construction recipe (the document's own serialized feature program — sketch geometry with constraints, then the solid features built on it; lengths are millimeters unless a unit is written):

FEATURE [Sketcher::SketchObject] Sketch118
  ArcFitTolerance = 0
  AttachmentSupport = -> [XZ_Plane064]
  ExternalBSplineMaxDegree = 0
  ExternalBSplineTolerance = 0
  FullyConstrained = true
  InternalTolerance = 1e-06
  MakeInternals = false
  MapMode = 5
  Placement = pos=(0,0,0) rot=(1,0,0;1.5708rad)
  Support = -> [XZ_Plane064]
  TreeRank = 0
  sketch-geometry (12):
    g0: LineSegment StartX=-6 StartY=2.67e-14 StartZ=0 EndX=-7 EndY=-1.177e-13 EndZ=0
    g1: LineSegment StartX=-7 StartY=-1.177e-13 StartZ=0 EndX=-7 EndY=4 EndZ=0
    g2: LineSegment StartX=-7 StartY=4 StartZ=0 EndX=-6 EndY=4 EndZ=0
    g3: LineSegment StartX=-6 StartY=4 StartZ=0 EndX=-6 EndY=3.6 EndZ=0
    g4: LineSegment StartX=-6 StartY=3.6 StartZ=0 EndX=-5 EndY=3.6 EndZ=0
    g5: LineSegment StartX=-5 StartY=3.6 StartZ=0 EndX=-5 EndY=4 EndZ=0
    g6: LineSegment StartX=-5 StartY=4 StartZ=0 EndX=-4 EndY=4 EndZ=0
    g7: LineSegment StartX=-4 StartY=4 StartZ=0 EndX=-4 EndY=0 EndZ=0
    g8: LineSegment StartX=-4 StartY=0 StartZ=0 EndX=-5 EndY=0 EndZ=0
    g9: LineSegment StartX=-5 StartY=0 StartZ=0 EndX=-5 EndY=0.4 EndZ=0
    g10: LineSegment StartX=-5 StartY=0.4 StartZ=0 EndX=-6 EndY=0.4 EndZ=0
    g11: LineSegment StartX=-6 StartY=0.4 StartZ=0 EndX=-6 EndY=2.67e-14 EndZ=0
  constraints (36):
    c: PointOnObject(g0,g-1)
    c: PointOnObject(g0,g-1)
    c: Coincident(g0,g1)
    c: Vertical(g1)
    c: Coincident(g1,g2)
    c: Horizontal(g2)
    c: Coincident(g2,g3)
    c: Vertical(g3)
    c: Coincident(g3,g4)
    c: Horizontal(g4)
    c: Coincident(g4,g5)
    c: Vertical(g5)
    c: Coincident(g5,g6)
    c: Horizontal(g6)
    c: Coincident(g6,g7)
    c: PointOnObject(g7,g-1)
    c: Vertical(g7)
    c: Coincident(g7,g8)
    c: PointOnObject(g8,g-1)
    c: Coincident(g8,g9)
    c: Vertical(g9)
    c: Coincident(g9,g10)
    c: Horizontal(g10)
    c: Coincident(g10,g11)
    c: Coincident(g11,g0)
    c: Vertical(g11)
    c: DistanceX(g7) = -4
    c: DistanceX(g0) = -7
    c: Equal(g8,g0)
    c: Equal(g2,g6)
    c: Equal(g4,g10)
    c: Equal(g3,g11)
    c: DistanceY(g3,g3) = 0.4
    c: DistanceX(g8,g8) = 1
    c: DistanceY(g1,g1) = 4
    c: PointOnObject(g2,g6)
FEATURE [PartDesign::Revolution] Revolution007
  AddSubType = 0
  Angle = 360
  Axis = (0,-2e-16,1)
  Base = (0,0,0)
  ClaimChildren = false
  Fit = 0
  FitJoin = 0
  InnerFit = 0
  InnerFitJoin = 0
  NewSolid = false
  Placement = pos=(0,0,0) rot=(1,0,0;1.5708rad)
  Profile = -> Sketch118
  ReferenceAxis = -> Sketch118 [V_Axis]
  Refine = true
  Suppress = false
  TreeRank = 0
  _ProfileBasedVersion = 0
FEATURE [PartDesign::Body] Body054  label="CoreMR148"
  AutoGroupSolids = false
  ClaimAllChildren = false
  ExportMode = 0
  Group = -> [Sketch118,Revolution007]
  Origin = -> Origin081
  SingleSolid = true
  Tip = -> Revolution007
  TreeRank = 0
  _ExportChildren = -> [Revolution007]
  _GroupVersion = 1
FEATURE [Sketcher::SketchObject] Sketch119
  ArcFitTolerance = 0
  AttachmentSupport = -> [XZ_Plane065]
  ExternalBSplineMaxDegree = 0
  ExternalBSplineTolerance = 0
  FullyConstrained = true
  InternalTolerance = 1e-06
  MakeInternals = false
  MapMode = 5
  Placement = pos=(0,0,0) rot=(1,0,0;1.5708rad)
  Support = -> [XZ_Plane065]
  TreeRank = 0
  sketch-geometry (4):
    g0: LineSegment StartX=-6 StartY=4 StartZ=0 EndX=-5 EndY=4 EndZ=0
    g1: LineSegment StartX=-5 StartY=4 StartZ=0 EndX=-5 EndY=0 EndZ=0
    g2: LineSegment StartX=-5 StartY=0 StartZ=0 EndX=-6 EndY=0 EndZ=0
    g3: LineSegment StartX=-6 StartY=0 StartZ=0 EndX=-6 EndY=4 EndZ=0
  constraints (12):
    c: Coincident(g0,g1)
    c: Coincident(g1,g2)
    c: Coincident(g2,g3)
    c: Coincident(g3,g0)
    c: Horizontal(g0)
    c: Horizontal(g2)
    c: Vertical(g1)
    c: Vertical(g3)
    c: PointOnObject(g1,g-1)
    c: DistanceY(g3,g3) = 4
    c: DistanceX(g1) = -5
    c: DistanceX(g2) = -6
FEATURE [PartDesign::Revolution] Revolution008
  AddSubType = 0
  Angle = 360
  Axis = (0,-2e-16,1)
  Base = (0,0,0)
  ClaimChildren = false
  Fit = 0
  FitJoin = 0
  InnerFit = 0
  InnerFitJoin = 0
  NewSolid = false
  Placement = pos=(0,0,0) rot=(1,0,0;1.5708rad)
  Profile = -> Sketch119
  ReferenceAxis = -> Sketch119 [V_Axis]
  Refine = true
  Suppress = false
  TreeRank = 0
  _ProfileBasedVersion = 0
FEATURE [PartDesign::Body] Body055  label="Sleeve"
  AutoGroupSolids = false
  ClaimAllChildren = false
  ExportMode = 0
  Group = -> [Sketch119,Revolution008]
  Origin = -> Origin082
  SingleSolid = true
  Tip = -> Revolution008
  TreeRank = 0
  _ExportChildren = -> [Revolution008]
  _GroupVersion = 1
COMPONENT P14 — recipe-attached ("YDLidar G2", modeled in this document).
Construction recipe (the document's own serialized feature program — sketch geometry with constraints, then the solid features built on it; lengths are millimeters unless a unit is written):

FEATURE [Sketcher::SketchObject] Sketch196
  ArcFitTolerance = 0
  AttachmentSupport = -> [XZ_Plane111]
  ExternalBSplineMaxDegree = 0
  ExternalBSplineTolerance = 0
  FullyConstrained = true
  InternalTolerance = 1e-06
  MakeInternals = false
  MapMode = 5
  Placement = pos=(0,0,0) rot=(1,0,0;1.5708rad)
  Support = -> [XZ_Plane111]
  TreeRank = 121
  sketch-geometry (8):
    g0: LineSegment StartX=0 StartY=0 StartZ=0 EndX=36.85 EndY=0 EndZ=0
    g1: LineSegment StartX=36.85 StartY=0 StartZ=0 EndX=36.3694 EndY=21.5 EndZ=0
    g2: LineSegment StartX=36.3694 StartY=21.5 StartZ=0 EndX=34.3694 EndY=21.5 EndZ=0
    g3: LineSegment StartX=34.3694 StartY=21.5 StartZ=0 EndX=34.3694 EndY=22.5 EndZ=0
    g4: LineSegment StartX=34.3694 StartY=22.5 StartZ=0 EndX=0 EndY=22.5 EndZ=0
    g5: LineSegment StartX=0 StartY=22.5 StartZ=0 EndX=0 EndY=0 EndZ=0
    g6: LineSegment [constr] StartX=36.3694 StartY=21.5 StartZ=0 EndX=35.9 EndY=42.5 EndZ=0
    g7: LineSegment [constr] StartX=35.9 StartY=42.5 StartZ=0 EndX=0 EndY=42.5 EndZ=0
  constraints (23):
    c: Coincident(g-1,g0)
    c: PointOnObject(g0,g-1)
    c: Coincident(g0,g1)
    c: Coincident(g1,g2)
    c: Horizontal(g2)
    c: Coincident(g2,g3)
    c: Vertical(g3)
    c: Coincident(g3,g4)
    c: Horizontal(g4)
    c: Coincident(g4,g5)
    c: Coincident(g5,g0)
    c: Vertical(g5)
    c: DistanceX(g0,g0) = 36.85
    c: Coincident(g6,g1)
    c: Coincident(g7,g6)
    c: Horizontal(g7)
    c: DistanceY(g7) = 42.5
    c: Parallel(g6,g1)
    c: DistanceX(g7,g7) = 35.9
    c: DistanceY(g1) = 21.5
    c: DistanceY(g3,g3) = 1
    c: DistanceX(g2,g2) = 2
    c: PointOnObject(g7,g-2)
FEATURE [PartDesign::Revolution] Revolution017
  AddSubType = 0
  Angle = 360
  Axis = (0,-2e-16,1)
  Base = (0,0,0)
  ClaimChildren = false
  Fit = 0
  FitJoin = 0
  InnerFit = 0
  InnerFitJoin = 0
  NewSolid = false
  Placement = pos=(0,0,0) rot=(1,0,0;1.5708rad)
  Profile = -> Sketch196
  ReferenceAxis = -> Sketch196 [V_Axis]
  Refine = true
  Reversed = true
  Suppress = false
  TreeRank = 0
  _ProfileBasedVersion = 1
FEATURE [PartDesign::Body] Body092  label="Base G2"
  AutoGroupSolids = false
  ClaimAllChildren = false
  ExportMode = 0
  Group = -> [Sketch196,Revolution017]
  Origin = -> Origin183
  SingleSolid = true
  Tip = -> Revolution017
  TreeRank = 0
  _ExportChildren = -> [Revolution017]
  _GroupVersion = 1
FEATURE [PartDesign::SubShapeBinder] Binder  label="Binder(Sketch004)"
  BindCopyOnChange = 0
  BindMode = 0
  ClaimChildren = false
  Context = -> Group011 [Part002.Body093.Binder.]
  EdgeTolerance = 1e-06
  FillStyle = 0
  Fuse = false
  MakeFace = true
  MergeEdges = true
  OffsetFill = false
  OffsetIntersection = false
  OffsetJoinType = 0
  OffsetOpenResult = false
  Outline = false
  PartialLoad = false
  Refine = true
  Relative = true
  SplitEdges = false
  Support = -> [Body092[Sketch196.]]
  TightBound = false
  TreeRank = 0
  _Version = 8
FEATURE [Sketcher::SketchObject] Sketch197
  ArcFitTolerance = 0
  AttachmentSupport = -> [XZ_Plane112]
  ExternalBSplineMaxDegree = 0
  ExternalBSplineTolerance = 0
  FullyConstrained = false
  InternalTolerance = 1e-06
  MakeInternals = false
  MapMode = 5
  Placement = pos=(0,0,0) rot=(1,0,0;1.5708rad)
  Support = -> [XZ_Plane112]
  TreeRank = 128
  sketch-geometry (4):
    g0: LineSegment StartX=0 StartY=22.5 StartZ=0 EndX=36.3471 EndY=22.5 EndZ=0
    g1: LineSegment StartX=36.3471 StartY=22.5 StartZ=0 EndX=35.9 EndY=42.5 EndZ=0
    g2: LineSegment StartX=35.9 StartY=42.5 StartZ=0 EndX=0 EndY=42.5 EndZ=0
    g3: LineSegment StartX=0 StartY=42.5 StartZ=0 EndX=0 EndY=22.5 EndZ=0
  constraints (8):
    c: Horizontal(g0)
    c: Coincident(g0,g1)
    c: Coincident(g1,g2)
    c: PointOnObject(g2,g-2)
    c: Horizontal(g2)
    c: Coincident(g2,g3)
    c: Coincident(g3,g0)
    c: DistanceY(g2) = 42.5
FEATURE [PartDesign::Revolution] Revolution001
  AddSubType = 0
  Angle = 360
  Axis = (0,-2e-16,1)
  Base = (0,0,0)
  ClaimChildren = false
  Fit = 0
  FitJoin = 0
  InnerFit = 0
  InnerFitJoin = 0
  NewSolid = false
  Placement = pos=(0,0,0) rot=(1,0,0;1.5708rad)
  Profile = -> Sketch197
  ReferenceAxis = -> Sketch197 [V_Axis]
  Refine = true
  Reversed = true
  Suppress = false
  TreeRank = 0
  _ProfileBasedVersion = 1
FEATURE [PartDesign::Fillet] Fillet047
  AddSubType = 0
  Base = -> Revolution001 [Edge2]
  BaseFeature = -> Revolution001
  NewSolid = false
  Placement = pos=(0,0,0) rot=(1,0,0;1.5708rad)
  Radius = 7
  Refine = true
  SupportTransform = false
  Suppress = false
  TreeRank = 0
FEATURE [Sketcher::SketchObject] Sketch198
  ArcFitTolerance = 0
  AttachmentOffset = pos=(0,0,25) rot=(0,0,1;0rad)
  AttachmentSupport = -> [XZ_Plane112]
  ExternalBSplineMaxDegree = 0
  ExternalBSplineTolerance = 0
  FullyConstrained = false
  InternalTolerance = 1e-06
  MakeInternals = false
  MapMode = 5
  Placement = pos=(0,-25,-5.6e-15) rot=(1,0,0;1.5708rad)
  Support = -> [XZ_Plane112]
  TreeRank = 129
  sketch-geometry (2):
    g0: Circle CenterX=-16.1575 CenterY=33.1 CenterZ=0 NormalX=0 NormalY=0 NormalZ=1 AngleXU=0 Radius=4.03782
    g1: Circle CenterX=16.1575 CenterY=33.1 CenterZ=0 NormalX=0 NormalY=0 NormalZ=1 AngleXU=0 Radius=4.91935
  constraints (2):
    c: DistanceY(g0) = 33.1
    c: Symmetric(g1,g0,g-2)
FEATURE [PartDesign::Pocket] Pocket063
  AddSubType = 1
  AutoTaperInnerAngle = false
  BaseFeature = -> Fillet047
  CheckUpToFaceLimits = true
  ClaimChildren = false
  Fit = 0
  FitJoin = 0
  InnerFit = 0
  InnerFitJoin = 0
  Length = 5
  Length2 = 100
  Linearize = true
  NewSolid = false
  Placement = pos=(0,0,0) rot=(1,0,0;1.5708rad)
  Profile = -> Sketch198
  Refine = true
  Reversed = true
  Suppress = false
  TaperInnerAngle = 0
  TaperInnerAngleRev = 0
  TreeRank = 0
  Type = 1
  _ProfileBasedVersion = 1
  _Version = 1
FEATURE [PartDesign::Body] Body093  label="Head G2"
  AutoGroupSolids = false
  ClaimAllChildren = false
  ExportMode = 0
  Group = -> [Binder,Sketch197,Revolution001,Fillet047,Sketch198,Pocket063]
  Origin = -> Origin007
  SingleSolid = true
  Tip = -> Pocket063
  TreeRank = 0
  _ExportChildren = -> [Binder,Revolution001,Fillet047,Pocket063]
  _GroupVersion = 1
FEATURE [Sketcher::SketchObject] Sketch199
  ArcFitTolerance = 0
  AttachmentSupport = -> [XY_Plane113]
  ExternalBSplineMaxDegree = 0
  ExternalBSplineTolerance = 0
  FullyConstrained = true
  InternalTolerance = 1e-06
  MakeInternals = false
  MapMode = 5
  Support = -> [XY_Plane113]
  TreeRank = 136
  sketch-geometry (1):
    g0: Circle CenterX=0 CenterY=0 CenterZ=0 NormalX=0 NormalY=0 NormalZ=1 AngleXU=0 Radius=1000
  constraints (2):
    c: Coincident(g0,g-1)
    c: Diameter(g0) = 2000
FEATURE [PartDesign::Pad] Pad080
  AddSubType = 0
  AlongSketchNormal = false
  AutoTaperInnerAngle = false
  CheckUpToFaceLimits = true
  ClaimChildren = false
  Direction = (0,0,1)
  Fit = 0
  FitJoin = 0
  InnerFit = 0
  InnerFitJoin = 0
  Length = 1
  Length2 = 100
  Linearize = true
  NewSolid = false
  Profile = -> Sketch199
  Refine = true
  Suppress = false
  TaperInnerAngle = 0
  TaperInnerAngleRev = 0
  TreeRank = 12
  Type = 0
  _ProfileBasedVersion = 1
FEATURE [PartDesign::Body] Body094  label="Field"
  AutoGroupSolids = false
  ClaimAllChildren = false
  ExportMode = 0
  Group = -> [Sketch199,Pad080]
  Origin = -> Origin184
  Placement = pos=(0,0,32.5) rot=(0,0,1;0rad)
  SingleSolid = true
  Tip = -> Pad080
  TreeRank = 10
  _ExportChildren = -> [Pad080]
  _GroupVersion = 1
COMPONENT P15 — recipe-attached ("LD06", modeled in this document).
Construction recipe (the document's own serialized feature program — sketch geometry with constraints, then the solid features built on it; lengths are millimeters unless a unit is written):

FEATURE [Sketcher::SketchObject] Sketch189
  ArcFitTolerance = 0
  AttachmentSupport = -> [XY_Plane109]
  ExternalBSplineMaxDegree = 0
  ExternalBSplineTolerance = 0
  FullyConstrained = true
  InternalTolerance = 1e-06
  MakeInternals = false
  MapMode = 5
  Support = -> [XY_Plane109]
  TreeRank = 58
  sketch-geometry (10):
    g0: ArcOfCircle CenterX=-14.1 CenterY=14.1 CenterZ=0 NormalX=0 NormalY=0 NormalZ=1 AngleXU=0 Radius=5.195 StartAngle=1.5708 EndAngle=3.14159
    g1: LineSegment StartX=-14.1 StartY=19.295 StartZ=0 EndX=14.1 EndY=19.295 EndZ=0
    g2: ArcOfCircle CenterX=14.1 CenterY=14.1 CenterZ=0 NormalX=0 NormalY=0 NormalZ=1 AngleXU=0 Radius=5.195 StartAngle=6.5809e-12 EndAngle=1.5708
    g3: LineSegment StartX=19.295 StartY=14.1 StartZ=0 EndX=19.295 EndY=-14.1 EndZ=0
    g4: ArcOfCircle CenterX=14.1 CenterY=-14.1 CenterZ=0 NormalX=0 NormalY=0 NormalZ=1 AngleXU=0 Radius=5.195 StartAngle=4.71239 EndAngle=6.28319
    g5: LineSegment StartX=14.1 StartY=-19.295 StartZ=0 EndX=-14.1 EndY=-19.295 EndZ=0
    g6: ArcOfCircle CenterX=-14.1 CenterY=-14.1 CenterZ=0 NormalX=0 NormalY=0 NormalZ=1 AngleXU=0 Radius=5.195 StartAngle=3.14159 EndAngle=4.71239
    g7: LineSegment StartX=-19.295 StartY=-14.1 StartZ=0 EndX=-19.295 EndY=14.1 EndZ=0
    g8: GeomPoint [constr] X=-19.295 Y=19.295 Z=0
    g9: GeomPoint [constr] X=19.295 Y=-19.295 Z=0
  constraints (23):
    c: Tangent(g0,g1) = 1.5708
    c: Tangent(g1,g2) = 1.5708
    c: Tangent(g2,g3) = 1.5708
    c: Tangent(g3,g4) = 1.5708
    c: Tangent(g4,g5) = 1.5708
    c: Tangent(g5,g6) = 1.5708
    c: Tangent(g6,g7) = 1.5708
    c: Tangent(g7,g0) = 1.5708
    c: Horizontal(g1)
    c: Horizontal(g5)
    c: Vertical(g3)
    c: Vertical(g7)
    c: Equal(g0,g2)
    c: Equal(g2,g4)
    c: Equal(g4,g6)
    c: PointOnObject(g8,g1)
    c: PointOnObject(g8,g7)
    c: PointOnObject(g9,g3)
    c: PointOnObject(g9,g5)
    c: Symmetric(g0,g4,g-1)
    c: Equal(g1,g3)
    c: DistanceY(g4,g1) = 38.59
    c: DistanceX(g0,g2) = 28.2
FEATURE [PartDesign::Pad] Pad077
  AddSubType = 0
  AlongSketchNormal = false
  AutoTaperInnerAngle = false
  CheckUpToFaceLimits = true
  ClaimChildren = false
  Direction = (0,0,1)
  Fit = 0
  FitJoin = 0
  InnerFit = 0
  InnerFitJoin = 0
  Length = 20.7
  Length2 = 100
  Linearize = true
  NewSolid = false
  Profile = -> Sketch189
  Refine = true
  Suppress = false
  TaperAngle = -2
  TaperInnerAngle = 0
  TaperInnerAngleRev = 0
  TreeRank = 59
  Type = 0
  _ProfileBasedVersion = 1
FEATURE [Sketcher::SketchObject] Sketch190
  ArcFitTolerance = 0
  AttachmentSupport = -> [Pad077]
  ExternalBSplineMaxDegree = 0
  ExternalBSplineTolerance = 0
  FullyConstrained = true
  InternalTolerance = 1e-06
  MakeInternals = false
  MapMode = 5
  Placement = pos=(0,0,20.7) rot=(0,0,1;0rad)
  Support = -> [Pad077]
  TreeRank = 60
  sketch-geometry (1):
    g0: Circle CenterX=0 CenterY=0 CenterZ=0 NormalX=0 NormalY=0 NormalZ=1 AngleXU=0 Radius=17.645
  constraints (2):
    c: Coincident(g0,g-1)
    c: Diameter(g0) = 35.29
FEATURE [PartDesign::Pad] Pad078
  AddSubType = 0
  AlongSketchNormal = false
  AutoTaperInnerAngle = false
  BaseFeature = -> Pad077
  CheckUpToFaceLimits = true
  ClaimChildren = false
  Direction = (0,0,1)
  Fit = 0
  FitJoin = 0
  InnerFit = 0
  InnerFitJoin = 0
  Length = 12.8
  Length2 = 100
  Linearize = true
  NewSolid = false
  Profile = -> Sketch190
  Refine = true
  Suppress = false
  TaperAngle = -1.5
  TaperInnerAngle = 0
  TaperInnerAngleRev = 0
  TreeRank = 61
  Type = 0
  _ProfileBasedVersion = 1
FEATURE [Sketcher::SketchObject] Sketch191
  ArcFitTolerance = 0
  AttachmentOffset = pos=(0,0,17) rot=(0,0,1;0rad)
  AttachmentSupport = -> [XZ_Plane109]
  ExternalBSplineMaxDegree = 0
  ExternalBSplineTolerance = 0
  FullyConstrained = true
  InternalTolerance = 1e-06
  MakeInternals = false
  MapMode = 5
  Placement = pos=(0,-17,-3.8e-15) rot=(1,0,0;1.5708rad)
  Support = -> [XZ_Plane109]
  TreeRank = 62
  sketch-geometry (5):
    g0: LineSegment StartX=-5 StartY=6.3 StartZ=0 EndX=-5 EndY=1.3 EndZ=0
    g1: LineSegment StartX=-5 StartY=1.3 StartZ=0 EndX=5 EndY=1.3 EndZ=0
    g2: LineSegment StartX=5 StartY=1.3 StartZ=0 EndX=5 EndY=6.3 EndZ=0
    g3: LineSegment StartX=5 StartY=6.3 StartZ=0 EndX=-5 EndY=6.3 EndZ=0
    g4: GeomPoint [constr] X=1.3758e-12 Y=3.8 Z=0
  constraints (13):
    c: Coincident(g0,g1)
    c: Coincident(g1,g2)
    c: Coincident(g2,g3)
    c: Coincident(g3,g0)
    c: Horizontal(g1)
    c: Horizontal(g3)
    c: Vertical(g0)
    c: Vertical(g2)
    c: Symmetric(g1,g0,g4)
    c: PointOnObject(g4,g-2)
    c: DistanceX(g3,g3) = 10
    c: DistanceY(g2,g2) = 5
    c: DistanceY(g-1,g4) = 3.8
FEATURE [PartDesign::Pocket] Pocket061
  AddSubType = 1
  AutoTaperInnerAngle = false
  BaseFeature = -> Pad078
  CheckUpToFaceLimits = true
  ClaimChildren = false
  Fit = 0
  FitJoin = 0
  InnerFit = 0
  InnerFitJoin = 0
  Length = 5
  Length2 = 100
  Linearize = true
  NewSolid = false
  Profile = -> Sketch191
  Refine = true
  Reversed = true
  Suppress = false
  TaperInnerAngle = 0
  TaperInnerAngleRev = 0
  TreeRank = 64
  Type = 1
  _ProfileBasedVersion = 1
  _Version = 1
FEATURE [Sketcher::SketchObject] Sketch192
  ArcFitTolerance = 0
  AttachmentSupport = -> [Pocket061]
  ExternalBSplineMaxDegree = 0
  ExternalBSplineTolerance = 0
  FullyConstrained = false
  InternalTolerance = 1e-06
  MakeInternals = false
  MapMode = 5
  Placement = pos=(0,-17,0) rot=(1,0,0;1.5708rad)
  Support = -> [Pocket061]
  TreeRank = 65
  sketch-geometry (8):
    g0: Circle CenterX=-2.295 CenterY=3.8 CenterZ=0 NormalX=0 NormalY=0 NormalZ=1 AngleXU=0 Radius=0.765
    g1: Circle CenterX=-0.765 CenterY=3.8 CenterZ=0 NormalX=0 NormalY=0 NormalZ=1 AngleXU=0 Radius=0.765
    g2: Circle CenterX=0.765 CenterY=3.8 CenterZ=0 NormalX=0 NormalY=0 NormalZ=1 AngleXU=0 Radius=0.765
    g3: Circle CenterX=2.295 CenterY=3.8 CenterZ=0 NormalX=0 NormalY=0 NormalZ=1 AngleXU=0 Radius=0.765
    g4: LineSegment [constr] StartX=-2.295 StartY=3.8 StartZ=0 EndX=-0.765 EndY=3.8 EndZ=0
    g5: LineSegment [constr] StartX=-0.765 StartY=3.8 StartZ=0 EndX=0.765 EndY=3.8 EndZ=0
    g6: LineSegment [constr] StartX=0.765 StartY=3.8 StartZ=0 EndX=2.295 EndY=3.8 EndZ=0
    g7: GeomPoint [constr] X=1.8986e-12 Y=3.8 Z=0
  constraints (16):
    c: Horizontal(g3,g2)
    c: Symmetric(g1,g2,g-2)
    c: Symmetric(g0,g3,g-2)
    c: Coincident(g4,g0)
    c: Coincident(g4,g1)
    c: Coincident(g5,g1)
    c: Coincident(g5,g2)
    c: Coincident(g6,g2)
    c: Coincident(g6,g3)
    c: Equal(g6,g5)
    c: PointOnObject(g7,g5)
    c: Equal(g0,g1)
    c: Equal(g1,g2)
    c: Equal(g2,g3)
    c: Tangent(g3,g2)
    c: DistanceX(g4,g4) = 1.53
FEATURE [PartDesign::Pad] Pad079
  AddSubType = 0
  AlongSketchNormal = false
  AutoTaperInnerAngle = false
  BaseFeature = -> Pocket061
  CheckUpToFaceLimits = true
  ClaimChildren = false
  Direction = (0,-1,2e-16)
  Fit = 0
  FitJoin = 0
  InnerFit = 0
  InnerFitJoin = 0
  Length = 10
  Length2 = 100
  Linearize = true
  NewSolid = false
  Profile = -> Sketch192
  Refine = true
  Suppress = false
  TaperInnerAngle = 0
  TaperInnerAngleRev = 0
  TreeRank = 66
  Type = 0
  _ProfileBasedVersion = 1
FEATURE [PartDesign::Fillet] Fillet045
  AddSubType = 0
  Base = -> Pad079 [Edge36]
  BaseFeature = -> Pad079
  NewSolid = false
  Radius = 1
  Refine = true
  SupportTransform = false
  Suppress = false
  TreeRank = 67
FEATURE [PartDesign::Fillet] Fillet046
  AddSubType = 0
  Base = -> Fillet045 [Edge13]
  BaseFeature = -> Fillet045
  NewSolid = false
  Radius = 1
  Refine = true
  SupportTransform = false
  Suppress = false
  TreeRank = 68
FEATURE [Sketcher::SketchObject] Sketch193
  ArcFitTolerance = 0
  AttachmentSupport = -> [Fillet046]
  ExternalBSplineMaxDegree = 0
  ExternalBSplineTolerance = 0
  FullyConstrained = true
  InternalTolerance = 1e-06
  MakeInternals = false
  MapMode = 5
  Placement = pos=(0,0,33.5) rot=(0,0,1;0rad)
  Support = -> [Fillet046]
  TreeRank = 69
  sketch-geometry (3):
    g0: LineSegment StartX=13 StartY=-0.866025 StartZ=0 EndX=13 EndY=0.866025 EndZ=0
    g1: LineSegment StartX=13 StartY=0.866025 StartZ=0 EndX=14.5 EndY=-2.501e-11 EndZ=0
    g2: LineSegment StartX=14.5 StartY=-2.501e-11 StartZ=0 EndX=13 EndY=-0.866025 EndZ=0
  constraints (9):
    c: Vertical(g0)
    c: Coincident(g0,g1)
    c: PointOnObject(g1,g-1)
    c: Coincident(g1,g2)
    c: Coincident(g2,g0)
    c: Equal(g2,g1)
    c: Equal(g1,g0)
    c: DistanceX(g-1,g0) = 13
    c: DistanceX(g0,g1) = 1.5
FEATURE [PartDesign::Pocket] Pocket062
  AddSubType = 1
  AutoTaperInnerAngle = false
  BaseFeature = -> Fillet046
  CheckUpToFaceLimits = true
  ClaimChildren = false
  Fit = 0
  FitJoin = 0
  InnerFit = 0
  InnerFitJoin = 0
  Length = 1
  Length2 = 100
  Linearize = true
  NewSolid = false
  Profile = -> Sketch193
  Refine = true
  Suppress = false
  TaperInnerAngle = 0
  TaperInnerAngleRev = 0
  TreeRank = 70
  Type = 0
  _ProfileBasedVersion = 1
  _Version = 1
FEATURE [Sketcher::SketchObject] Sketch195
  ArcFitTolerance = 0
  AttachmentOffset = pos=(0,0,21.7) rot=(0,0,1;0rad)
  AttachmentSupport = -> [XY_Plane110]
  ExternalBSplineMaxDegree = 0
  ExternalBSplineTolerance = 0
  FullyConstrained = true
  InternalTolerance = 1e-06
  MakeInternals = false
  MapMode = 5
  Placement = pos=(0,0,21.7) rot=(0,0,1;0rad)
  Support = -> [XY_Plane110]
  TreeRank = 81
  sketch-geometry (2):
    g0: Circle CenterX=0 CenterY=0 CenterZ=0 NormalX=0 NormalY=0 NormalZ=1 AngleXU=0 Radius=20
    g1: Circle CenterX=0 CenterY=0 CenterZ=0 NormalX=0 NormalY=0 NormalZ=1 AngleXU=0 Radius=500
  constraints (4):
    c: Coincident(g0,g-1)
    c: Coincident(g1,g0)
    c: Diameter(g1) = 1000
    c: Diameter(g0) = 40
FEATURE [PartDesign::Pad] Pad013
  AddSubType = 0
  AlongSketchNormal = false
  AutoTaperInnerAngle = false
  CheckUpToFaceLimits = true
  ClaimChildren = false
  Direction = (0,0,1)
  Fit = 0
  FitJoin = 0
  InnerFit = 0
  InnerFitJoin = 0
  Length = 10
  Length2 = 100
  Linearize = true
  NewSolid = false
  Profile = -> Sketch195
  Refine = true
  Suppress = false
  TaperInnerAngle = 0
  TaperInnerAngleRev = 0
  TreeRank = 82
  Type = 0
  _ProfileBasedVersion = 1
FEATURE [PartDesign::Body] Body091  label="OpticalWindow"
  AutoGroupSolids = false
  ClaimAllChildren = false
  ExportMode = 0
  Group = -> [Sketch195,Pad013]
  Origin = -> Origin182
  SingleSolid = true
  Tip = -> Pad013
  TreeRank = 80
  _ExportChildren = -> [Pad013]
  _GroupVersion = 1
FEATURE [PartDesign::Body] Body090  label="BaseLD06"
  AutoGroupSolids = false
  ClaimAllChildren = false
  ExportMode = 0
  Group = -> [Sketch189,Pad077,Sketch190,Pad078,Sketch191,Pocket061,Sketch192,Pad079,Fillet045,Fillet046,Sketch193,Pocket062,Sketch194,Export,Export001,Pocket009,Pocket010]
  Origin = -> Origin181
  SingleSolid = true
  Tip = -> Pocket010
  TreeRank = 57
  _ExportChildren = -> [Pad077,Pad078,Pocket061,Pad079,Fillet045,Fillet046,Pocket062,Sketch194,Pocket009,Pocket010]
  _GroupVersion = 1
FEATURE [PartDesign::Pocket] Pocket010
  AddSubType = 1
  AutoTaperInnerAngle = false
  BaseFeature = -> Pocket009
  CheckUpToFaceLimits = true
  ClaimChildren = false
  Fit = 0
  FitJoin = 0
  InnerFit = 0
  InnerFitJoin = 0
  Length = 11.8
  Length2 = 100
  Linearize = true
  NewSolid = false
  Profile = -> Export
  Refine = true
  Suppress = false
  TaperInnerAngle = 0
  TaperInnerAngleRev = 0
  TreeRank = 170
  Type = 0
  _ProfileBasedVersion = 1
  _Version = 1
FEATURE [Sketcher::SketchObject] Sketch194
  ArcFitTolerance = 0
  AttachmentSupport = -> [XY_Plane109]
  Exports = -> [Export,Export001]
  ExternalBSplineMaxDegree = 0
  ExternalBSplineTolerance = 0
  FullyConstrained = true
  InternalTolerance = 1e-06
  MakeInternals = false
  MapMode = 5
  Placement = pos=(0,0,0) rot=(0,1,0;3.14159rad)
  Support = -> [XY_Plane109]
  TreeRank = 84
  sketch-geometry (4):
    g0: Circle CenterX=-14.1 CenterY=14.1 CenterZ=0 NormalX=0 NormalY=0 NormalZ=1 AngleXU=0 Radius=2.4
    g1: Circle CenterX=14.1 CenterY=-14.1 CenterZ=0 NormalX=0 NormalY=0 NormalZ=1 AngleXU=0 Radius=2.4
    g2: Circle CenterX=-14.1 CenterY=14.1 CenterZ=0 NormalX=0 NormalY=0 NormalZ=1 AngleXU=0 Radius=1.225
    g3: Circle CenterX=14.1 CenterY=-14.1 CenterZ=0 NormalX=0 NormalY=0 NormalZ=1 AngleXU=0 Radius=1.225
  constraints (9):
    c: Symmetric(g0,g1,g-1)
    c: Equal(g0,g1)
    c: Diameter(g0) = 4.8
    c: DistanceX(g0,g-1) = 14.1
    c: DistanceY(g-1,g0) = 14.1
    c: Coincident(g2,g0)
    c: Coincident(g3,g1)
    c: Equal(g3,g2)
    c: Diameter(g3) = 2.45
FEATURE [Sketcher::SketchExport] Export
  Base = -> Sketch194
  BaseRefs = -> Sketch194 [edge1,edge2]
  Placement = pos=(0,0,0) rot=(0,1,0;3.14159rad)
  Refs = ;g2.edge1 | ;g3.edge2
  SyncPlacement = true
  TreeRank = 85
FEATURE [Sketcher::SketchExport] Export001
  Base = -> Sketch194
  BaseRefs = -> Sketch194 [edge3,edge4]
  Placement = pos=(0,0,0) rot=(0,1,0;3.14159rad)
  Refs = ;g4.edge3 | ;g5.edge4
  SyncPlacement = true
  TreeRank = 86
FEATURE [PartDesign::Pocket] Pocket009
  AddSubType = 1
  AutoTaperInnerAngle = false
  BaseFeature = -> Pocket062
  CheckUpToFaceLimits = true
  ClaimChildren = false
  Fit = 0
  FitJoin = 0
  InnerFit = 0
  InnerFitJoin = 0
  Length = 5
  Length2 = 100
  Linearize = true
  NewSolid = false
  Profile = -> Export001
  Refine = true
  Suppress = false
  TaperInnerAngle = 0
  TaperInnerAngleRev = 0
  TreeRank = 169
  Type = 1
  _ProfileBasedVersion = 1
  _Version = 1
COMPONENT P16 — recipe-attached ("MF128", modeled in this document).
Construction recipe (the document's own serialized feature program — sketch geometry with constraints, then the solid features built on it; lengths are millimeters unless a unit is written):

FEATURE [Sketcher::SketchObject] Sketch116
  ArcFitTolerance = 0
  AttachmentSupport = -> [XY_Plane062]
  ExternalBSplineMaxDegree = 0
  ExternalBSplineTolerance = 0
  FullyConstrained = true
  InternalTolerance = 1e-06
  MakeInternals = false
  MapMode = 5
  Support = -> [XY_Plane062]
  TreeRank = 0
  sketch-geometry (10):
    g0: LineSegment StartX=-6.8 StartY=0 StartZ=0 EndX=-6.8 EndY=0.8 EndZ=0
    g1: LineSegment StartX=-6.8 StartY=0.8 StartZ=0 EndX=-5.4 EndY=0.8 EndZ=0
    g2: LineSegment StartX=-5.4 StartY=0.8 StartZ=0 EndX=-5.4 EndY=-2.7 EndZ=0
    g3: LineSegment StartX=-5.4 StartY=-2.7 StartZ=0 EndX=-6 EndY=-2.7 EndZ=0
    g4: LineSegment StartX=-6 StartY=-2.7 StartZ=0 EndX=-6 EndY=0 EndZ=0
    g5: LineSegment StartX=-6 StartY=0 StartZ=0 EndX=-6.8 EndY=0 EndZ=0
    g6: LineSegment StartX=-4.6 StartY=0.8 StartZ=0 EndX=-4 EndY=0.8 EndZ=0
    g7: LineSegment StartX=-4 StartY=0.8 StartZ=0 EndX=-4 EndY=-2.7 EndZ=0
    g8: LineSegment StartX=-4 StartY=-2.7 StartZ=0 EndX=-4.6 EndY=-2.7 EndZ=0
    g9: LineSegment StartX=-4.6 StartY=-2.7 StartZ=0 EndX=-4.6 EndY=0.8 EndZ=0
  constraints (30):
    c: Vertical(g0)
    c: Coincident(g0,g1)
    c: Horizontal(g1)
    c: Coincident(g1,g2)
    c: Vertical(g2)
    c: Coincident(g2,g3)
    c: Horizontal(g3)
    c: Coincident(g3,g4)
    c: Vertical(g4)
    c: Coincident(g4,g5)
    c: Coincident(g5,g0)
    c: Horizontal(g5)
    c: Coincident(g6,g7)
    c: Coincident(g7,g8)
    c: Coincident(g8,g9)
    c: Coincident(g9,g6)
    c: Horizontal(g6)
    c: Horizontal(g8)
    c: Vertical(g7)
    c: Vertical(g9)
    c: PointOnObject(g6,g1)
    c: PointOnObject(g4,g-1)
    c: DistanceY(g2,g2) = 3.5
    c: PointOnObject(g8,g3)
    c: DistanceX(g3) = -6
    c: DistanceX(g6) = -4
    c: Equal(g3,g6)
    c: DistanceX(g6,g6) = 0.6
    c: DistanceX(g0) = -6.8
    c: DistanceY(g0,g0) = 0.8
FEATURE [PartDesign::Revolution] Revolution005
  AddSubType = 0
  Angle = 360
  Axis = (0,1,0)
  Base = (0,0,0)
  ClaimChildren = false
  Fit = 0
  FitJoin = 0
  InnerFit = 0
  InnerFitJoin = 0
  NewSolid = false
  Profile = -> Sketch116
  ReferenceAxis = -> Sketch116 [V_Axis]
  Refine = true
  Suppress = false
  TreeRank = 0
  _ProfileBasedVersion = 1
FEATURE [PartDesign::Body] Body052  label="CoreMF128"
  AutoGroupSolids = false
  ClaimAllChildren = false
  ExportMode = 0
  Group = -> [Sketch116,Revolution005]
  Origin = -> Origin016
  Tip = -> Revolution005
  TreeRank = 0
  _ExportChildren = -> [Revolution005]
  _GroupVersion = 1
FEATURE [Sketcher::SketchObject] Sketch117
  ArcFitTolerance = 0
  AttachmentSupport = -> [XY_Plane063]
  ExternalBSplineMaxDegree = 0
  ExternalBSplineTolerance = 0
  FullyConstrained = true
  InternalTolerance = 1e-06
  MakeInternals = false
  MapMode = 5
  Support = -> [XY_Plane063]
  TreeRank = 0
  sketch-geometry (4):
    g0: LineSegment StartX=-5.5 StartY=0.55 StartZ=0 EndX=-4.5 EndY=0.55 EndZ=0
    g1: LineSegment StartX=-4.5 StartY=0.55 StartZ=0 EndX=-4.5 EndY=-2.45 EndZ=0
    g2: LineSegment StartX=-4.5 StartY=-2.45 StartZ=0 EndX=-5.5 EndY=-2.45 EndZ=0
    g3: LineSegment StartX=-5.5 StartY=-2.45 StartZ=0 EndX=-5.5 EndY=0.55 EndZ=0
  constraints (12):
    c: Coincident(g0,g1)
    c: Coincident(g1,g2)
    c: Coincident(g2,g3)
    c: Coincident(g3,g0)
    c: Horizontal(g0)
    c: Horizontal(g2)
    c: Vertical(g1)
    c: Vertical(g3)
    c: DistanceY(g3,g3) = 3
    c: DistanceX(g0,g0) = 1
    c: DistanceX(g0,g-1) = 4.5
    c: DistanceY(g-1,g0) = 0.55
FEATURE [PartDesign::Revolution] Revolution006
  AddSubType = 0
  Angle = 360
  Axis = (0,1,0)
  Base = (0,0,0)
  ClaimChildren = false
  Fit = 0
  FitJoin = 0
  InnerFit = 0
  InnerFitJoin = 0
  NewSolid = false
  Profile = -> Sketch117
  ReferenceAxis = -> Sketch117 [V_Axis]
  Refine = true
  Suppress = false
  TreeRank = 0
  _ProfileBasedVersion = 1
FEATURE [PartDesign::Body] Body053  label="SleeveMF128"
  AutoGroupSolids = false
  ClaimAllChildren = false
  ExportMode = 0
  Group = -> [Sketch117,Revolution006]
  Origin = -> Origin080
  SingleSolid = true
  Tip = -> Revolution006
  TreeRank = 0
  _ExportChildren = -> [Revolution006]
  _GroupVersion = 1
COMPONENT P17 — recipe-attached ("MF83", modeled in this document).
Construction recipe (the document's own serialized feature program — sketch geometry with constraints, then the solid features built on it; lengths are millimeters unless a unit is written):

FEATURE [Sketcher::SketchObject] Sketch160
  ArcFitTolerance = 0
  AttachmentSupport = -> [XY_Plane091]
  ExternalBSplineMaxDegree = 0
  ExternalBSplineTolerance = 0
  FullyConstrained = true
  InternalTolerance = 1e-06
  MakeInternals = false
  MapMode = 5
  Support = -> [XY_Plane091]
  TreeRank = 0
  sketch-geometry (10):
    g0: LineSegment StartX=-4.6 StartY=0 StartZ=0 EndX=-4.6 EndY=0.6 EndZ=0
    g1: LineSegment StartX=-4.6 StartY=0.6 StartZ=0 EndX=-3.4 EndY=0.6 EndZ=0
    g2: LineSegment StartX=-3.4 StartY=0.6 StartZ=0 EndX=-3.4 EndY=-2.4 EndZ=0
    g3: LineSegment StartX=-3.4 StartY=-2.4 StartZ=0 EndX=-4 EndY=-2.4 EndZ=0
    g4: LineSegment StartX=-4 StartY=-2.4 StartZ=0 EndX=-4 EndY=0 EndZ=0
    g5: LineSegment StartX=-4 StartY=0 StartZ=0 EndX=-4.6 EndY=0 EndZ=0
    g6: LineSegment StartX=-2.1 StartY=0.6 StartZ=0 EndX=-1.5 EndY=0.6 EndZ=0
    g7: LineSegment StartX=-1.5 StartY=0.6 StartZ=0 EndX=-1.5 EndY=-2.4 EndZ=0
    g8: LineSegment StartX=-1.5 StartY=-2.4 StartZ=0 EndX=-2.1 EndY=-2.4 EndZ=0
    g9: LineSegment StartX=-2.1 StartY=-2.4 StartZ=0 EndX=-2.1 EndY=0.6 EndZ=0
  constraints (30):
    c: Vertical(g0)
    c: Coincident(g0,g1)
    c: Horizontal(g1)
    c: Coincident(g1,g2)
    c: Vertical(g2)
    c: Coincident(g2,g3)
    c: Horizontal(g3)
    c: Coincident(g3,g4)
    c: Vertical(g4)
    c: Coincident(g4,g5)
    c: Coincident(g5,g0)
    c: Horizontal(g5)
    c: Coincident(g6,g7)
    c: Coincident(g7,g8)
    c: Coincident(g8,g9)
    c: Coincident(g9,g6)
    c: Horizontal(g6)
    c: Horizontal(g8)
    c: Vertical(g7)
    c: Vertical(g9)
    c: PointOnObject(g6,g1)
    c: PointOnObject(g4,g-1)
    c: DistanceY(g2,g2) = 3
    c: PointOnObject(g8,g3)
    c: DistanceX(g3) = -4
    c: DistanceX(g6) = -1.5
    c: Equal(g3,g6)
    c: DistanceX(g6,g6) = 0.6
    c: DistanceX(g0) = -4.6
    c: DistanceY(g0,g0) = 0.6
FEATURE [PartDesign::Revolution] Revolution010
  AddSubType = 0
  Angle = 360
  Axis = (0,1,0)
  Base = (0,0,0)
  ClaimChildren = false
  Fit = 0
  FitJoin = 0
  InnerFit = 0
  InnerFitJoin = 0
  NewSolid = false
  Profile = -> Sketch160
  ReferenceAxis = -> Sketch160 [V_Axis]
  Refine = true
  Suppress = false
  TreeRank = 0
  _ProfileBasedVersion = 1
FEATURE [PartDesign::Body] Body074  label="CoreMF83"
  AutoGroupSolids = false
  ClaimAllChildren = false
  ExportMode = 0
  Group = -> [Sketch160,Revolution010]
  Origin = -> Origin158
  Placement = pos=(0,2.84e-14,0) rot=(0,0,1;0rad)
  Tip = -> Revolution010
  TreeRank = 0
  _ExportChildren = -> [Revolution010]
  _GroupVersion = 1
FEATURE [Sketcher::SketchObject] Sketch161
  ArcFitTolerance = 0
  AttachmentSupport = -> [XY_Plane092]
  ExternalBSplineMaxDegree = 0
  ExternalBSplineTolerance = 0
  FullyConstrained = true
  InternalTolerance = 1e-06
  MakeInternals = false
  MapMode = 5
  Support = -> [XY_Plane092]
  TreeRank = 0
  sketch-geometry (4):
    g0: LineSegment StartX=-3.4 StartY=0.5 StartZ=0 EndX=-2.1 EndY=0.5 EndZ=0
    g1: LineSegment StartX=-2.1 StartY=0.5 StartZ=0 EndX=-2.1 EndY=-2.3 EndZ=0
    g2: LineSegment StartX=-2.1 StartY=-2.3 StartZ=0 EndX=-3.4 EndY=-2.3 EndZ=0
    g3: LineSegment StartX=-3.4 StartY=-2.3 StartZ=0 EndX=-3.4 EndY=0.5 EndZ=0
  constraints (12):
    c: Coincident(g0,g1)
    c: Coincident(g1,g2)
    c: Coincident(g2,g3)
    c: Coincident(g3,g0)
    c: Horizontal(g0)
    c: Horizontal(g2)
    c: Vertical(g1)
    c: Vertical(g3)
    c: DistanceY(g3,g3) = 2.8
    c: DistanceX(g0,g0) = 1.3
    c: DistanceX(g0,g-1) = 2.1
    c: DistanceY(g-1,g0) = 0.5
FEATURE [PartDesign::Revolution] Revolution011
  AddSubType = 0
  Angle = 360
  Axis = (1e-16,1,-1e-16)
  Base = (0,0,0)
  ClaimChildren = false
  Fit = 0
  FitJoin = 0
  InnerFit = 0
  InnerFitJoin = 0
  NewSolid = false
  Profile = -> Sketch161
  ReferenceAxis = -> Y_Axis092
  Refine = true
  Suppress = false
  TreeRank = 0
  _ProfileBasedVersion = 1
FEATURE [PartDesign::Body] Body075  label="SleeveMF83"
  AutoGroupSolids = false
  ClaimAllChildren = false
  ExportMode = 0
  Group = -> [Sketch161,Revolution011]
  Origin = -> Origin159
  Placement = pos=(0,2.84e-14,0) rot=(0,0,1;0rad)
  SingleSolid = true
  Tip = -> Revolution011
  TreeRank = 0
  _ExportChildren = -> [Revolution011]
  _GroupVersion = 1
COMPONENT P18 — recipe-attached ("633ZZ", modeled in this document).
Construction recipe (the document's own serialized feature program — sketch geometry with constraints, then the solid features built on it; lengths are millimeters unless a unit is written):

FEATURE [Sketcher::SketchObject] Sketch169
  ArcFitTolerance = 0
  AttachmentSupport = -> [XZ_Plane100]
  ExternalBSplineMaxDegree = 0
  ExternalBSplineTolerance = 0
  FullyConstrained = true
  InternalTolerance = 1e-06
  MakeInternals = false
  MapMode = 5
  Placement = pos=(0,0,0) rot=(1,0,0;1.5708rad)
  Support = -> [XZ_Plane100]
  TreeRank = 0
  sketch-geometry (12):
    g0: LineSegment StartX=-5.5 StartY=1.2718e-12 StartZ=0 EndX=-6.5 EndY=1.052e-12 EndZ=0
    g1: LineSegment StartX=-6.5 StartY=1.052e-12 StartZ=0 EndX=-6.5 EndY=5 EndZ=0
    g2: LineSegment StartX=-6.5 StartY=5 StartZ=0 EndX=-5.5 EndY=5 EndZ=0
    g3: LineSegment StartX=-5.5 StartY=5 StartZ=0 EndX=-5.5 EndY=4.6 EndZ=0
    g4: LineSegment StartX=-5.5 StartY=4.6 StartZ=0 EndX=-2.5 EndY=4.6 EndZ=0
    g5: LineSegment StartX=-2.5 StartY=4.6 StartZ=0 EndX=-2.5 EndY=5 EndZ=0
    g6: LineSegment StartX=-2.5 StartY=5 StartZ=0 EndX=-1.5 EndY=5 EndZ=0
    g7: LineSegment StartX=-1.5 StartY=5 StartZ=0 EndX=-1.5 EndY=0 EndZ=0
    g8: LineSegment StartX=-1.5 StartY=0 StartZ=0 EndX=-2.5 EndY=0 EndZ=0
    g9: LineSegment StartX=-2.5 StartY=0 StartZ=0 EndX=-2.5 EndY=0.4 EndZ=0
    g10: LineSegment StartX=-2.5 StartY=0.4 StartZ=0 EndX=-5.5 EndY=0.4 EndZ=0
    g11: LineSegment StartX=-5.5 StartY=0.4 StartZ=0 EndX=-5.5 EndY=1.2718e-12 EndZ=0
  constraints (36):
    c: PointOnObject(g0,g-1)
    c: PointOnObject(g0,g-1)
    c: Coincident(g0,g1)
    c: Vertical(g1)
    c: Coincident(g1,g2)
    c: Horizontal(g2)
    c: Coincident(g2,g3)
    c: Vertical(g3)
    c: Coincident(g3,g4)
    c: Horizontal(g4)
    c: Coincident(g4,g5)
    c: Vertical(g5)
    c: Coincident(g5,g6)
    c: Horizontal(g6)
    c: Coincident(g6,g7)
    c: PointOnObject(g7,g-1)
    c: Vertical(g7)
    c: Coincident(g7,g8)
    c: PointOnObject(g8,g-1)
    c: Coincident(g8,g9)
    c: Vertical(g9)
    c: Coincident(g9,g10)
    c: Horizontal(g10)
    c: Coincident(g10,g11)
    c: Coincident(g11,g0)
    c: Vertical(g11)
    c: DistanceX(g7) = -1.5
    c: DistanceX(g0) = -6.5
    c: Equal(g8,g0)
    c: Equal(g2,g6)
    c: Equal(g4,g10)
    c: Equal(g3,g11)
    c: DistanceY(g3,g3) = 0.4
    c: DistanceX(g8,g8) = 1
    c: DistanceY(g1,g1) = 5
    c: PointOnObject(g2,g6)
FEATURE [PartDesign::Revolution] Revolution012
  AddSubType = 0
  Angle = 360
  Axis = (0,-2e-16,1)
  Base = (0,0,0)
  ClaimChildren = false
  Fit = 0
  FitJoin = 0
  InnerFit = 0
  InnerFitJoin = 0
  NewSolid = false
  Placement = pos=(0,0,0) rot=(1,0,0;1.5708rad)
  Profile = -> Sketch169
  ReferenceAxis = -> Sketch169 [V_Axis]
  Refine = true
  Suppress = false
  TreeRank = 0
  _ProfileBasedVersion = 0
FEATURE [PartDesign::Body] Body080  label="CoreMR149"
  AutoGroupSolids = false
  ClaimAllChildren = false
  ExportMode = 0
  Group = -> [Sketch169,Revolution012]
  Origin = -> Origin166
  SingleSolid = true
  Tip = -> Revolution012
  TreeRank = 94
  _ExportChildren = -> [Revolution012]
  _GroupVersion = 1
FEATURE [Sketcher::SketchObject] Sketch170
  ArcFitTolerance = 0
  AttachmentSupport = -> [XZ_Plane101]
  ExternalBSplineMaxDegree = 0
  ExternalBSplineTolerance = 0
  FullyConstrained = true
  InternalTolerance = 1e-06
  MakeInternals = false
  MapMode = 5
  Placement = pos=(0,0,0) rot=(1,0,0;1.5708rad)
  Support = -> [XZ_Plane101]
  TreeRank = 0
  sketch-geometry (4):
    g0: LineSegment StartX=-5.5 StartY=5 StartZ=0 EndX=-2.5 EndY=5 EndZ=0
    g1: LineSegment StartX=-2.5 StartY=5 StartZ=0 EndX=-2.5 EndY=0 EndZ=0
    g2: LineSegment StartX=-2.5 StartY=3e-16 StartZ=0 EndX=-5.5 EndY=3e-16 EndZ=0
    g3: LineSegment StartX=-5.5 StartY=3e-16 StartZ=0 EndX=-5.5 EndY=5 EndZ=0
  constraints (12):
    c: Coincident(g0,g1)
    c: Coincident(g1,g2)
    c: Coincident(g2,g3)
    c: Coincident(g3,g0)
    c: Horizontal(g0)
    c: Horizontal(g2)
    c: Vertical(g1)
    c: Vertical(g3)
    c: PointOnObject(g1,g-1)
    c: DistanceY(g3,g3) = 5
    c: DistanceX(g1) = -2.5
    c: DistanceX(g2) = -5.5
FEATURE [PartDesign::Revolution] Revolution013
  AddSubType = 0
  Angle = 360
  Axis = (0,-2e-16,1)
  Base = (0,0,0)
  ClaimChildren = false
  Fit = 0
  FitJoin = 0
  InnerFit = 0
  InnerFitJoin = 0
  NewSolid = false
  Placement = pos=(0,0,0) rot=(1,0,0;1.5708rad)
  Profile = -> Sketch170
  ReferenceAxis = -> Sketch170 [V_Axis]
  Refine = true
  Suppress = false
  TreeRank = 0
  _ProfileBasedVersion = 0
FEATURE [PartDesign::Body] Body081  label="Sleeve001"
  AutoGroupSolids = false
  ClaimAllChildren = false
  ExportMode = 0
  Group = -> [Sketch170,Revolution013]
  Origin = -> Origin167
  SingleSolid = true
  Tip = -> Revolution013
  TreeRank = 95
  _ExportChildren = -> [Revolution013]
  _GroupVersion = 1
COMPONENT P19 — recipe-attached ("BAU-2195813", modeled in this document).
Construction recipe (the document's own serialized feature program — sketch geometry with constraints, then the solid features built on it; lengths are millimeters unless a unit is written):

FEATURE [Sketcher::SketchObject] Sketch171
  ArcFitTolerance = 0
  AttachmentSupport = -> [XY_Plane102]
  ExternalBSplineMaxDegree = 0
  ExternalBSplineTolerance = 0
  FullyConstrained = true
  InternalTolerance = 1e-06
  MakeInternals = false
  MapMode = 5
  Support = -> [XY_Plane102]
  TreeRank = 111
  sketch-geometry (1):
    g0: Circle CenterX=0 CenterY=0 CenterZ=0 NormalX=0 NormalY=0 NormalZ=1 AngleXU=0 Radius=9
  constraints (2):
    c: Coincident(g0,g-1)
    c: Diameter(g0) = 18
FEATURE [PartDesign::Pad] Pad073
  AddSubType = 0
  AlongSketchNormal = false
  AutoTaperInnerAngle = false
  CheckUpToFaceLimits = true
  ClaimChildren = false
  Direction = (0,0,1)
  Fit = 0
  FitJoin = 0
  InnerFit = 0
  InnerFitJoin = 0
  Length = 9
  Length2 = 100
  Linearize = true
  NewSolid = false
  Profile = -> Sketch171
  Refine = true
  Suppress = false
  TaperInnerAngle = 0
  TaperInnerAngleRev = 0
  TreeRank = 112
  Type = 0
  _ProfileBasedVersion = 1
FEATURE [PartDesign::Fillet] Fillet041
  AddSubType = 0
  Base = -> Pad073 [Edge3]
  BaseFeature = -> Pad073
  NewSolid = false
  Radius = 0.4
  Refine = true
  SupportTransform = false
  Suppress = false
  TreeRank = 113
FEATURE [Sketcher::SketchObject] Sketch172
  ArcFitTolerance = 0
  AttachmentSupport = -> [XZ_Plane102]
  ExternalBSplineMaxDegree = 0
  ExternalBSplineTolerance = 0
  FullyConstrained = true
  InternalTolerance = 1e-06
  MakeInternals = false
  MapMode = 5
  Placement = pos=(0,0,0) rot=(1,0,0;1.5708rad)
  Support = -> [XZ_Plane102]
  TreeRank = 114
  sketch-geometry (8):
    g0: LineSegment StartX=0 StartY=-2.075e-13 StartZ=0 EndX=7.75 EndY=-2.075e-13 EndZ=0
    g1: LineSegment StartX=7.75 StartY=-2.075e-13 StartZ=0 EndX=7.75 EndY=-3 EndZ=0
    g2: LineSegment StartX=7.75 StartY=-3 StartZ=0 EndX=8.8 EndY=-3 EndZ=0
    g3: LineSegment StartX=8.8 StartY=-3 StartZ=0 EndX=8.8 EndY=-10.5 EndZ=0
    g4: LineSegment StartX=8.8 StartY=-10.5 StartZ=0 EndX=7.75 EndY=-10.5 EndZ=0
    g5: LineSegment StartX=7.75 StartY=-10.5 StartZ=0 EndX=7.75 EndY=-19 EndZ=0
    g6: LineSegment StartX=7.75 StartY=-19 StartZ=0 EndX=0 EndY=-19 EndZ=0
    g7: LineSegment StartX=0 StartY=-19 StartZ=0 EndX=0 EndY=-2.061e-13 EndZ=0
  constraints (23):
    c: Coincident(g-1,g0)
    c: Horizontal(g0)
    c: Coincident(g0,g1)
    c: Vertical(g1)
    c: Coincident(g1,g2)
    c: Horizontal(g2)
    c: Coincident(g2,g3)
    c: Vertical(g3)
    c: Coincident(g3,g4)
    c: Coincident(g4,g5)
    c: Vertical(g5)
    c: Coincident(g5,g6)
    c: PointOnObject(g6,g-2)
    c: Horizontal(g6)
    c: Coincident(g6,g7)
    c: Coincident(g7,g0)
    c: DistanceY(g1,g1) = 3
    c: DistanceX(g2) = 8.8
    c: DistanceX(g1) = 7.75
    c: PointOnObject(g5,g1)
    c: DistanceY(g3,g3) = 7.5
    c: Horizontal(g4)
    c: DistanceY(g7,g7) = 19
FEATURE [PartDesign::Revolution] Revolution014
  AddSubType = 0
  Angle = 360
  Axis = (0,2e-16,1)
  Base = (0,0,0)
  BaseFeature = -> Fillet041
  ClaimChildren = false
  Fit = 0
  FitJoin = 0
  InnerFit = 0
  InnerFitJoin = 0
  Linearize = true
  NewSolid = false
  Profile = -> Sketch172
  ReferenceAxis = -> Sketch172 [V_Axis]
  Refine = true
  Reversed = true
  Suppress = false
  TreeRank = 115
  _ProfileBasedVersion = 1
FEATURE [PartDesign::Body] Body082  label="MainBody"
  AutoGroupSolids = false
  ClaimAllChildren = false
  ExportMode = 0
  Group = -> [Sketch171,Pad073,Fillet041,Sketch172,Revolution014]
  Origin = -> Origin169
  SingleSolid = true
  Tip = -> Revolution014
  TreeRank = 110
  _ExportChildren = -> [Pad073,Fillet041,Revolution014]
  _GroupVersion = 1
FEATURE [Part::SubShapeBinder] Import002  label="Import002(Revolution014)"
  BindCopyOnChange = 0
  BindMode = 0
  ClaimChildren = false
  Context = -> Part036 [Body083.Import002.]
  EdgeTolerance = 1e-06
  FillStyle = 0
  Fuse = false
  MakeFace = false
  MergeEdges = true
  OffsetFill = false
  OffsetIntersection = false
  OffsetJoinType = 0
  OffsetOpenResult = false
  Outline = false
  PartialLoad = false
  Relative = true
  SplitEdges = false
  Support = -> [Body082[Revolution014.]]
  TightBound = false
  TreeRank = 127
  _Version = 8
FEATURE [Sketcher::SketchObject] Sketch173
  ArcFitTolerance = 0
  AttachmentSupport = -> [Import002]
  ExternalBSplineMaxDegree = 0
  ExternalBSplineTolerance = 0
  FullyConstrained = true
  InternalTolerance = 1e-06
  MakeInternals = false
  MapMode = 5
  Placement = pos=(0,-4.2e-15,-19) rot=(1,0,0;3.14159rad)
  Support = -> [Import002]
  TreeRank = 126
  sketch-geometry (5):
    g0: LineSegment StartX=9.5 StartY=9.5 StartZ=0 EndX=-9.5 EndY=9.5 EndZ=0
    g1: LineSegment StartX=-9.5 StartY=9.5 StartZ=0 EndX=-9.5 EndY=-9.5 EndZ=0
    g2: LineSegment StartX=-9.5 StartY=-9.5 StartZ=0 EndX=9.5 EndY=-9.5 EndZ=0
    g3: LineSegment StartX=9.5 StartY=-9.5 StartZ=0 EndX=9.5 EndY=9.5 EndZ=0
    g4: Circle [constr] CenterX=-1.2948e-12 CenterY=-4.7939e-12 CenterZ=0 NormalX=0 NormalY=0 NormalZ=1 AngleXU=0 Radius=13.435
  constraints (14):
    c: Coincident(g0,g1)
    c: Coincident(g1,g2)
    c: Coincident(g2,g3)
    c: Coincident(g3,g0)
    c: Equal(g0,g1)
    c: Equal(g0,g2)
    c: Equal(g0,g3)
    c: PointOnObject(g0,g4)
    c: PointOnObject(g1,g4)
    c: PointOnObject(g2,g4)
    c: PointOnObject(g3,g4)
    c: Coincident(g4,g-1)
    c: Horizontal(g0)
    c: DistanceX(g0,g0) = 19
FEATURE [PartDesign::Pad] Pad074
  AddSubType = 0
  AlongSketchNormal = false
  AutoTaperInnerAngle = false
  CheckUpToFaceLimits = true
  ClaimChildren = false
  Direction = (0,-2e-16,-1)
  Fit = 0
  FitJoin = 0
  InnerFit = 0
  InnerFitJoin = 0
  Length = 14.5
  Length2 = 100
  Linearize = true
  NewSolid = false
  Profile = -> Sketch173
  Refine = true
  Suppress = false
  TaperInnerAngle = 0
  TaperInnerAngleRev = 0
  TreeRank = 128
  Type = 0
  _ProfileBasedVersion = 1
FEATURE [PartDesign::Fillet] Fillet042
  AddSubType = 0
  Base = -> Pad074 [Edge11,Edge6]
  BaseFeature = -> Pad074
  NewSolid = false
  Radius = 1
  Refine = true
  SupportTransform = false
  Suppress = false
  TreeRank = 129
FEATURE [PartDesign::Body] Body083  label="ElectronicBody"
  AutoGroupSolids = false
  ClaimAllChildren = false
  ExportMode = 0
  Group = -> [Sketch173,Import002,Pad074,Fillet042]
  Origin = -> Origin170
  SingleSolid = true
  Tip = -> Fillet042
  TreeRank = 125
  _ExportChildren = -> [Import002,Pad074,Fillet042]
  _GroupVersion = 1
FEATURE [Part::SubShapeBinder] Import003  label="Import003(Fillet042)"
  BindCopyOnChange = 0
  BindMode = 0
  ClaimChildren = false
  Context = -> Part036 [Body084.Import003.]
  EdgeTolerance = 1e-06
  FillStyle = 0
  Fuse = false
  MakeFace = false
  MergeEdges = true
  OffsetFill = false
  OffsetIntersection = false
  OffsetJoinType = 0
  OffsetOpenResult = false
  Outline = false
  PartialLoad = false
  Relative = true
  SplitEdges = false
  Support = -> [Body083[Fillet042.]]
  TightBound = false
  TreeRank = 141
  _Version = 8
FEATURE [Sketcher::SketchObject] Sketch174
  ArcFitTolerance = 0
  AttachmentSupport = -> [Import003]
  ExternalBSplineMaxDegree = 0
  ExternalBSplineTolerance = 0
  FullyConstrained = true
  InternalTolerance = 1e-06
  MakeInternals = false
  MapMode = 5
  Placement = pos=(0,-1.25e-14,-33.5) rot=(1,0,0;3.14159rad)
  Support = -> [Import003]
  TreeRank = 140
  sketch-geometry (16):
    g0: LineSegment StartX=-7.75 StartY=7.3 StartZ=0 EndX=-7.25 EndY=7.3 EndZ=0
    g1: LineSegment StartX=-7.25 StartY=7.3 StartZ=0 EndX=-7.25 EndY=4.5 EndZ=0
    g2: LineSegment StartX=-7.25 StartY=4.5 StartZ=0 EndX=-7.75 EndY=4.5 EndZ=0
    g3: LineSegment StartX=-7.75 StartY=4.5 StartZ=0 EndX=-7.75 EndY=7.3 EndZ=0
    g4: LineSegment StartX=7.25 StartY=7.3 StartZ=0 EndX=7.75 EndY=7.3 EndZ=0
    g5: LineSegment StartX=7.75 StartY=7.3 StartZ=0 EndX=7.75 EndY=4.5 EndZ=0
    g6: LineSegment StartX=7.75 StartY=4.5 StartZ=0 EndX=7.25 EndY=4.5 EndZ=0
    g7: LineSegment StartX=7.25 StartY=4.5 StartZ=0 EndX=7.25 EndY=7.3 EndZ=0
    g8: LineSegment StartX=7.25 StartY=-4.5 StartZ=0 EndX=7.75 EndY=-4.5 EndZ=0
    g9: LineSegment StartX=7.75 StartY=-4.5 StartZ=0 EndX=7.75 EndY=-7.3 EndZ=0
    g10: LineSegment StartX=7.75 StartY=-7.3 StartZ=0 EndX=7.25 EndY=-7.3 EndZ=0
    g11: LineSegment StartX=7.25 StartY=-7.3 StartZ=0 EndX=7.25 EndY=-4.5 EndZ=0
    g12: LineSegment StartX=-7.75 StartY=-4.5 StartZ=0 EndX=-7.25 EndY=-4.5 EndZ=0
    g13: LineSegment StartX=-7.25 StartY=-4.5 StartZ=0 EndX=-7.25 EndY=-7.3 EndZ=0
    g14: LineSegment StartX=-7.25 StartY=-7.3 StartZ=0 EndX=-7.75 EndY=-7.3 EndZ=0
    g15: LineSegment StartX=-7.75 StartY=-7.3 StartZ=0 EndX=-7.75 EndY=-4.5 EndZ=0
  constraints (46):
    c: Coincident(g0,g1)
    c: Coincident(g1,g2)
    c: Coincident(g2,g3)
    c: Coincident(g3,g0)
    c: Horizontal(g0)
    c: Horizontal(g2)
    c: Vertical(g1)
    c: Vertical(g3)
    c: DistanceX(g1,g-1) = 7.25
    c: DistanceX(g0,g0) = 0.5
    c: DistanceY(g3,g3) = 2.8
    c: DistanceY(g2) = 4.5
    c: Coincident(g4,g5)
    c: Coincident(g5,g6)
    c: Coincident(g6,g7)
    c: Coincident(g7,g4)
    c: Horizontal(g4)
    c: Horizontal(g6)
    c: Vertical(g5)
    c: Vertical(g7)
    c: Coincident(g8,g9)
    c: Coincident(g9,g10)
    c: Coincident(g10,g11)
    c: Coincident(g11,g8)
    c: Horizontal(g8)
    c: Horizontal(g10)
    c: Vertical(g9)
    c: Vertical(g11)
    c: Coincident(g12,g13)
    c: Coincident(g13,g14)
    c: Coincident(g14,g15)
    c: Coincident(g15,g12)
    c: Horizontal(g12)
    c: Horizontal(g14)
    c: Vertical(g13)
    c: Vertical(g15)
    c: Equal(g12,g8)
    c: Equal(g8,g6)
    c: Equal(g6,g2)
    c: Equal(g1,g7)
    c: Equal(g7,g11)
    c: Equal(g11,g13)
    c: Horizontal(g13,g10)
    c: Vertical(g8,g5)
    c: Symmetric(g0,g4,g-2)
    c: Symmetric(g12,g1,g-1)
FEATURE [PartDesign::Pad] Pad075
  AddSubType = 0
  AlongSketchNormal = false
  AutoTaperInnerAngle = false
  CheckUpToFaceLimits = true
  ClaimChildren = false
  Direction = (0,-4e-16,-1)
  Fit = 0
  FitJoin = 0
  InnerFit = 0
  InnerFitJoin = 0
  Length = 8.5
  Length2 = 100
  Linearize = true
  NewSolid = false
  Profile = -> Sketch174
  Refine = true
  Suppress = false
  TaperInnerAngle = 0
  TaperInnerAngleRev = 0
  TreeRank = 142
  Type = 0
  _ProfileBasedVersion = 1
FEATURE [PartDesign::Chamfer] Chamfer045
  AddSubType = 0
  Angle = 45
  Base = -> Pad075 [Edge46,Edge40,Edge34,Edge28,Edge16,Edge22,Edge10,Edge4]
  BaseFeature = -> Pad075
  ChamferType = 0
  FlipDirection = false
  NewSolid = false
  Refine = true
  Size = 0.6
  Size2 = 1
  SupportTransform = false
  Suppress = false
  TreeRank = 143
FEATURE [Sketcher::SketchObject] Sketch175
  ArcFitTolerance = 0
  AttachmentSupport = -> [YZ_Plane104]
  ExternalBSplineMaxDegree = 0
  ExternalBSplineTolerance = 0
  FullyConstrained = false
  InternalTolerance = 1e-06
  MakeInternals = false
  MapMode = 5
  Placement = pos=(0,0,0) rot=(0.57735,0.57735,0.57735;2.0944rad)
  Support = -> [YZ_Plane104]
  TreeRank = 144
  sketch-geometry (8):
    g0: ArcOfCircle CenterX=-6 CenterY=-38.7066 CenterZ=0 NormalX=0 NormalY=0 NormalZ=1 AngleXU=0 Radius=0.456793 StartAngle=1.3e-15 EndAngle=3.14159
    g1: ArcOfCircle CenterX=-6 CenterY=-40.4194 CenterZ=0 NormalX=0 NormalY=0 NormalZ=1 AngleXU=0 Radius=0.456793 StartAngle=3.14159 EndAngle=6.28319
    g2: LineSegment StartX=-6.45679 StartY=-38.7066 StartZ=0 EndX=-6.45679 EndY=-40.4194 EndZ=0
    g3: LineSegment StartX=-5.54321 StartY=-40.4194 StartZ=0 EndX=-5.54321 EndY=-38.7066 EndZ=0
    g4: ArcOfCircle CenterX=6 CenterY=-38.7066 CenterZ=0 NormalX=0 NormalY=0 NormalZ=1 AngleXU=0 Radius=0.417287 StartAngle=-5.3e-15 EndAngle=3.14159
    g5: ArcOfCircle CenterX=6 CenterY=-40.4194 CenterZ=0 NormalX=0 NormalY=0 NormalZ=1 AngleXU=0 Radius=0.417287 StartAngle=3.14159 EndAngle=6.28319
    g6: LineSegment StartX=5.58271 StartY=-38.7066 StartZ=0 EndX=5.58271 EndY=-40.4194 EndZ=0
    g7: LineSegment StartX=6.41729 StartY=-40.4194 StartZ=0 EndX=6.41729 EndY=-38.7066 EndZ=0
  constraints (14):
    c: Tangent(g0,g2) = -1.5708
    c: Tangent(g2,g1) = -1.5708
    c: Tangent(g1,g3) = -1.5708
    c: Tangent(g3,g0) = -1.5708
    c: Equal(g0,g1)
    c: Tangent(g4,g6) = -1.5708
    c: Tangent(g6,g5) = -1.5708
    c: Tangent(g5,g7) = -1.5708
    c: Tangent(g7,g4) = -1.5708
    c: Equal(g4,g5)
    c: Symmetric(g4,g0,g-2)
    c: Symmetric(g5,g1,g-2)
    c: Vertical(g1,g0)
    c: DistanceX(g0) = -6
FEATURE [PartDesign::Pocket] Pocket054
  AddSubType = 1
  AutoTaperInnerAngle = false
  BaseFeature = -> Chamfer045
  CheckUpToFaceLimits = true
  ClaimChildren = false
  Fit = 0
  FitJoin = 0
  InnerFit = 0
  InnerFitJoin = 0
  Length = 5
  Length2 = 100
  Linearize = true
  Midplane = true
  NewSolid = false
  Profile = -> Sketch175
  Refine = true
  Suppress = false
  TaperInnerAngle = 0
  TaperInnerAngleRev = 0
  TreeRank = 145
  Type = 1
  _ProfileBasedVersion = 1
  _Version = 1
FEATURE [PartDesign::Body] Body084  label="ElectronicPins"
  AutoGroupSolids = false
  ClaimAllChildren = false
  ExportMode = 0
  Group = -> [Sketch174,Import003,Pad075,Chamfer045,Sketch175,Pocket054]
  Origin = -> Origin171
  Tip = -> Pocket054
  TreeRank = 139
  _ExportChildren = -> [Import003,Pad075,Chamfer045,Pocket054]
  _GroupVersion = 1
FEATURE [Sketcher::SketchObject] Sketch176
  ArcFitTolerance = 0
  AttachmentSupport = -> [YZ_Plane105]
  ExternalBSplineMaxDegree = 0
  ExternalBSplineTolerance = 0
  FullyConstrained = true
  InternalTolerance = 1e-06
  MakeInternals = false
  MapMode = 5
  Placement = pos=(0,0,0) rot=(0.57735,0.57735,0.57735;2.0944rad)
  Support = -> [YZ_Plane105]
  TreeRank = 156
  sketch-geometry (12):
    g0: LineSegment StartX=-7.5 StartY=0 StartZ=0 EndX=-7.5 EndY=17 EndZ=0
    g1: LineSegment StartX=-7.5 StartY=17 StartZ=0 EndX=-12 EndY=17 EndZ=0
    g2: LineSegment StartX=-12 StartY=17 StartZ=0 EndX=-12 EndY=20 EndZ=0
    g3: LineSegment [constr] StartX=-7.5 StartY=0 StartZ=0 EndX=7.5 EndY=0 EndZ=0
    g4: LineSegment [constr] StartX=7.5 StartY=0 StartZ=0 EndX=7.5 EndY=17 EndZ=0
    g5: LineSegment [constr] StartX=7.5 StartY=17 StartZ=0 EndX=12 EndY=17 EndZ=0
    g6: LineSegment [constr] StartX=12 StartY=17 StartZ=0 EndX=12 EndY=20 EndZ=0
    g7: ArcOfCircle [constr] CenterX=-1.51e-14 CenterY=-51.5 CenterZ=0 NormalX=0 NormalY=0 NormalZ=1 AngleXU=0 Radius=72.5 StartAngle=1.40451 EndAngle=1.73708
    g8: GeomPoint [constr] X=4.5e-15 Y=21 Z=0
    g9: LineSegment StartX=0 StartY=0 StartZ=0 EndX=4.5e-15 EndY=21 EndZ=0
    g10: LineSegment StartX=-7.5 StartY=0 StartZ=0 EndX=0 EndY=0 EndZ=0
    g11: ArcOfCircle CenterX=-1.51e-14 CenterY=-51.5 CenterZ=0 NormalX=0 NormalY=0 NormalZ=1 AngleXU=0 Radius=72.5 StartAngle=1.5708 EndAngle=1.73708
  constraints (31):
    c: PointOnObject(g0,g-1)
    c: Vertical(g0)
    c: Coincident(g0,g1)
    c: Horizontal(g1)
    c: Coincident(g1,g2)
    c: Coincident(g0,g3)
    c: Coincident(g3,g4)
    c: Vertical(g4)
    c: Coincident(g4,g5)
    c: Horizontal(g5)
    c: Coincident(g5,g6)
    c: Vertical(g6)
    c: Vertical(g2)
    c: Equal(g6,g2)
    c: Symmetric(g0,g3,g-1)
    c: Symmetric(g6,g2,g-2)
    c: DistanceX(g0,g4) = 15
    c: DistanceY(g4) = 17
    c: DistanceY(g2,g2) = 3
    c: DistanceX(g1,g5) = 24
    c: Coincident(g7,g2)
    c: Coincident(g7,g6)
    c: PointOnObject(g8,g-2)
    c: Coincident(g9,g-1)
    c: Coincident(g9,g8)
    c: Coincident(g10,g0)
    c: Coincident(g10,g9)
    c: Coincident(g11,g7)
    c: Coincident(g11,g9)
    c: Coincident(g11,g2)
    c: DistanceY(g9) = 21
FEATURE [PartDesign::Revolution] Revolution015
  AddSubType = 0
  Angle = 360
  Axis = (-2e-16,3e-16,1)
  Base = (0,0,0)
  ClaimChildren = false
  Fit = 0
  FitJoin = 0
  InnerFit = 0
  InnerFitJoin = 0
  Linearize = true
  NewSolid = false
  Placement = pos=(0,0,0) rot=(0.57735,0.57735,0.57735;2.0944rad)
  Profile = -> Sketch176
  ReferenceAxis = -> Sketch176 [V_Axis]
  Refine = true
  Suppress = false
  TreeRank = 157
  _ProfileBasedVersion = 1
FEATURE [PartDesign::Fillet] Fillet043
  AddSubType = 0
  Base = -> Revolution015 [Edge5]
  BaseFeature = -> Revolution015
  NewSolid = false
  Placement = pos=(0,0,0) rot=(0.57735,0.57735,0.57735;2.0944rad)
  Radius = 1
  Refine = true
  SupportTransform = false
  Suppress = false
  TreeRank = 158
FEATURE [PartDesign::Body] Body085  label="ButtonCaps"
  AutoGroupSolids = false
  ClaimAllChildren = false
  ExportMode = 0
  Group = -> [Sketch176,Revolution015,Fillet043]
  Origin = -> Origin172
  SingleSolid = true
  Tip = -> Fillet043
  TreeRank = 155
  _ExportChildren = -> [Revolution015,Fillet043]
  _GroupVersion = 1
COMPONENT P20 — geometry summary ("ConnecteurPneu-Ressort"; no construction recipe available for this part):
  bounding box: 47.1 x 23.5 x 16.0 mm
  tessellated surface: 18,782 triangles
  volume: 3419 mm^3 (19% of its bounding box)
  symmetry: mirror-symmetric across its z mid-plane
